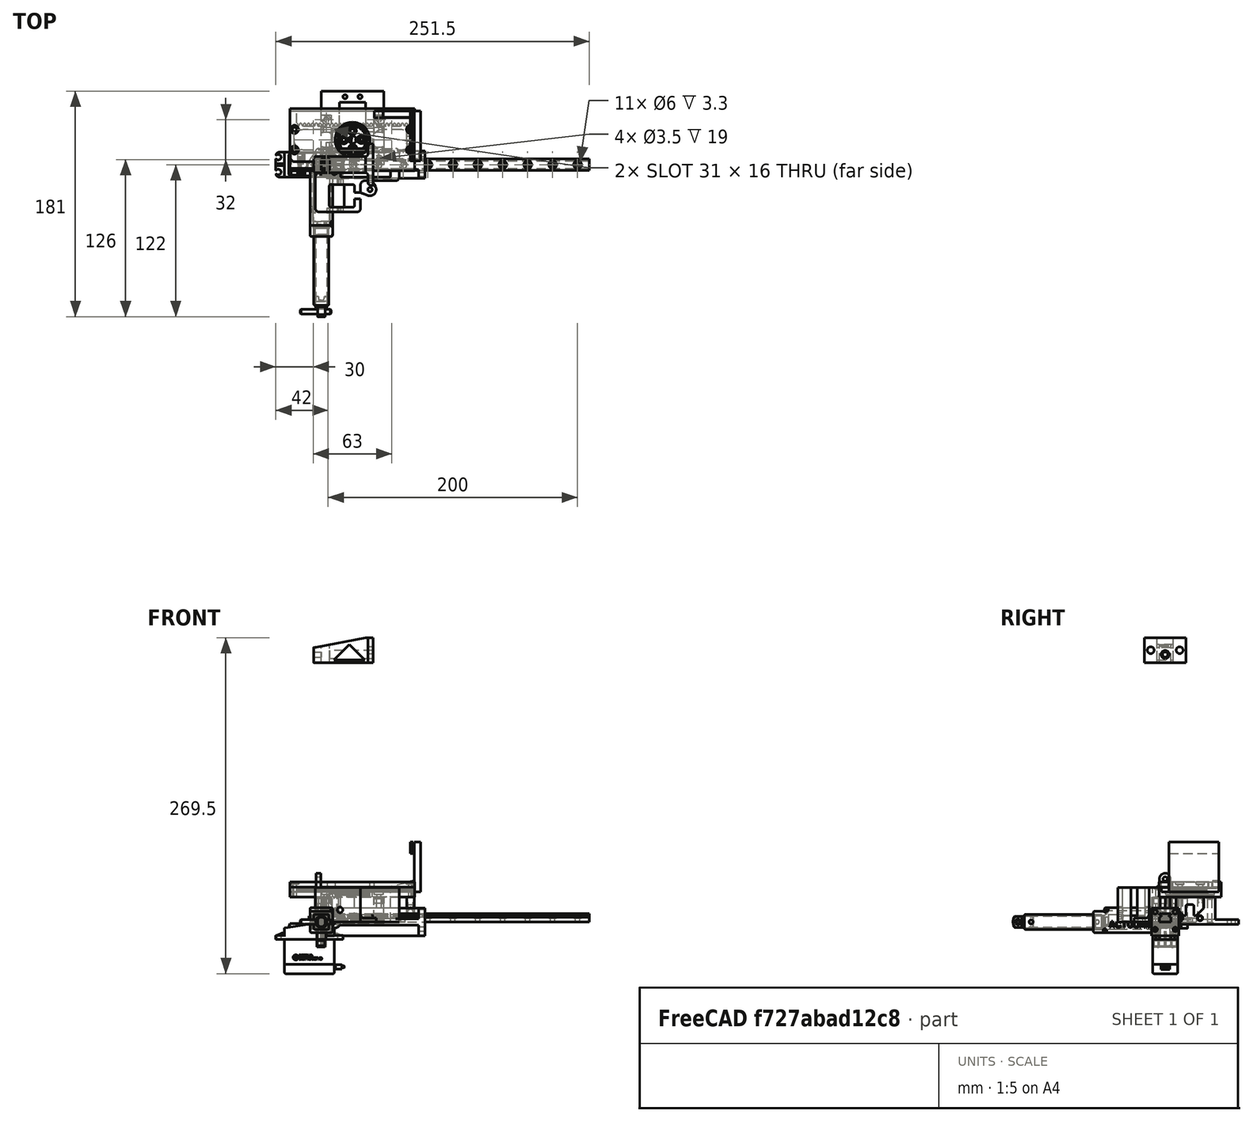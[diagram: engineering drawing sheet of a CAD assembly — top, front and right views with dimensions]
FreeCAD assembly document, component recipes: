
FREECAD ASSEMBLY — COMPONENT RECIPES ("PincePlanche")

This assembly document has 18 components, labeled P0..P17 below (a component is one placed body or linked part). 16 of them carry a construction recipe — the FreeCAD feature program that regenerates the part from scratch, quoted from this document or its linked companion documents; the rest are supplied as boundary geometry only. No exploded tour is included for this assembly.
COMPONENT P0 — recipe-attached ("support_pince_planche_bas", modeled in this document).
Construction recipe (the document's own serialized feature program — sketch geometry with constraints, then the solid features built on it; lengths are millimeters unless a unit is written):

FEATURE [Sketcher::SketchObject] Sketch042
  ArcFitTolerance = 1e-06
  AttachmentSupport = -> [XY_Plane019]
  FullyConstrained = true
  MakeInternals = false
  MapMode = 5
  Placement = pos=(0,0,0) rot=(0,1,0;3.14159rad)
  expr: Constraints[36] = 20 mm + VarSet.jeu
  expr: Constraints[37] = 40 mm + VarSet.jeu
  expr: Constraints[72] = 18 mm + VarSet.jeu
  expr: Constraints[73] = 20 mm + VarSet.jeu
  expr: Constraints[86] = 9 mm + VarSet.jeu
  expr: Constraints[87] = 6.5 mm + VarSet.jeu
  sketch-geometry (52):
    g0: LineSegment StartX=-28.5 StartY=-38 StartZ=0 EndX=1.8 EndY=-38 EndZ=0
    g1: LineSegment StartX=4.8 StartY=-35 StartZ=0 EndX=4.8 EndY=10 EndZ=0
    g2: ArcOfCircle CenterX=1.8 CenterY=-35 CenterZ=0 NormalX=0 NormalY=0 NormalZ=1 AngleXU=0 Radius=3 StartAngle=4.71239 EndAngle=6.28319
    g3: ArcOfCircle CenterX=1.8 CenterY=10 CenterZ=0 NormalX=0 NormalY=0 NormalZ=1 AngleXU=0 Radius=3 StartAngle=0 EndAngle=1.5708
    g4: GeomPoint [constr] X=4.8 Y=-38 Z=0
    g5: LineSegment StartX=-59.5 StartY=-13 StartZ=0 EndX=-34.5 EndY=-13 EndZ=0
    g6: LineSegment StartX=1.8 StartY=13 StartZ=0 EndX=-59.5 EndY=13 EndZ=0
    g7: ArcOfCircle CenterX=-59.5 CenterY=10 CenterZ=0 NormalX=0 NormalY=0 NormalZ=1 AngleXU=0 Radius=3 StartAngle=1.5708 EndAngle=3.14159
    g8: ArcOfCircle CenterX=-59.5 CenterY=-10 CenterZ=0 NormalX=0 NormalY=0 NormalZ=1 AngleXU=0 Radius=3 StartAngle=3.14159 EndAngle=4.71239
    g9: LineSegment StartX=-54.575 StartY=-10.075 StartZ=0 EndX=-16.425 EndY=-10.075 EndZ=0
    g10: LineSegment StartX=-15.425 StartY=-9.075 StartZ=0 EndX=-15.425 EndY=9.075 EndZ=0
    g11: LineSegment StartX=-16.425 StartY=10.075 StartZ=0 EndX=-54.575 EndY=10.075 EndZ=0
    g12: ArcOfCircle CenterX=-54.575 CenterY=9.075 CenterZ=0 NormalX=0 NormalY=0 NormalZ=1 AngleXU=0 Radius=1 StartAngle=1.5708 EndAngle=3.14159
    g13: ArcOfCircle CenterX=-54.575 CenterY=-9.075 CenterZ=0 NormalX=0 NormalY=0 NormalZ=1 AngleXU=0 Radius=1 StartAngle=3.14159 EndAngle=4.71239
    g14: ArcOfCircle CenterX=-16.425 CenterY=-9.075 CenterZ=0 NormalX=0 NormalY=0 NormalZ=1 AngleXU=0 Radius=1 StartAngle=4.71239 EndAngle=6.28319
    g15: ArcOfCircle CenterX=-16.425 CenterY=9.075 CenterZ=0 NormalX=0 NormalY=0 NormalZ=1 AngleXU=0 Radius=1 StartAngle=0 EndAngle=1.5708
    g16: GeomPoint [constr] X=-55.575 Y=10.075 Z=0
    g17: GeomPoint [constr] X=-15.425 Y=-10.075 Z=0
    g18: GeomPoint X=-35.5 Y=0 Z=0
    g19: ArcOfCircle CenterX=-34.5 CenterY=-16 CenterZ=0 NormalX=0 NormalY=0 NormalZ=1 AngleXU=0 Radius=3 StartAngle=0 EndAngle=1.5708
    g20: LineSegment StartX=-31.5 StartY=-16 StartZ=0 EndX=-31.5 EndY=-22.5 EndZ=0
    g21: ArcOfCircle CenterX=-28.5 CenterY=-35 CenterZ=0 NormalX=0 NormalY=0 NormalZ=1 AngleXU=0 Radius=3 StartAngle=3.14159 EndAngle=4.71239
    g22: GeomPoint [constr] X=-31.5 Y=-38 Z=0
    g23: GeomPoint X=-16.5 Y=-25 Z=0
    g24: LineSegment StartX=-26.575 StartY=-17.125 StartZ=0 EndX=-26.575 EndY=-22.5 EndZ=0
    g25: LineSegment StartX=-25.375 StartY=-34.075 StartZ=0 EndX=-7.625 EndY=-34.075 EndZ=0
    g26: LineSegment StartX=-6.425 StartY=-32.875 StartZ=0 EndX=-6.425 EndY=-17.125 EndZ=0
    g27: LineSegment StartX=-7.625 StartY=-15.925 StartZ=0 EndX=-25.375 EndY=-15.925 EndZ=0
    g28: ArcOfCircle CenterX=-25.375 CenterY=-17.125 CenterZ=0 NormalX=0 NormalY=0 NormalZ=1 AngleXU=0 Radius=1.2 StartAngle=1.5708 EndAngle=3.14159
    g29: ArcOfCircle CenterX=-25.375 CenterY=-32.875 CenterZ=0 NormalX=0 NormalY=0 NormalZ=1 AngleXU=0 Radius=1.2 StartAngle=3.14159 EndAngle=4.71239
    g30: ArcOfCircle CenterX=-7.625 CenterY=-32.875 CenterZ=0 NormalX=0 NormalY=0 NormalZ=1 AngleXU=0 Radius=1.2 StartAngle=4.71239 EndAngle=6.28319
    g31: ArcOfCircle CenterX=-7.625 CenterY=-17.125 CenterZ=0 NormalX=0 NormalY=0 NormalZ=1 AngleXU=0 Radius=1.2 StartAngle=-9e-16 EndAngle=1.5708
    g32: GeomPoint [constr] X=-26.575 Y=-15.925 Z=0
    g33: GeomPoint [constr] X=-6.425 Y=-34.075 Z=0
    g34: LineSegment StartX=-6.575 StartY=4.575 StartZ=0 EndX=-6.575 EndY=-4.575 EndZ=0
    g35: LineSegment StartX=-6.575 StartY=-4.575 StartZ=0 EndX=0.075 EndY=-4.575 EndZ=0
    g36: LineSegment StartX=0.075 StartY=-4.575 StartZ=0 EndX=0.075 EndY=4.575 EndZ=0
    g37: LineSegment StartX=0.075 StartY=4.575 StartZ=0 EndX=-6.575 EndY=4.575 EndZ=0
    g38: GeomPoint X=-3.25 Y=0 Z=0
    g39: LineSegment StartX=-26.575 StartY=-22.5 StartZ=0 EndX=-31.5 EndY=-22.5 EndZ=0
    g40: LineSegment StartX=-31.5 StartY=-27.5 StartZ=0 EndX=-26.575 EndY=-27.5 EndZ=0
    g41: LineSegment StartX=-26.575 StartY=-27.5 StartZ=0 EndX=-26.575 EndY=-32.875 EndZ=0
    g42: LineSegment StartX=-31.5 StartY=-27.5 StartZ=0 EndX=-31.5 EndY=-35 EndZ=0
    g43: LineSegment [constr] StartX=-16.5 StartY=-25 StartZ=0 EndX=-31.5 EndY=-25 EndZ=0
    g44: LineSegment StartX=-62.5 StartY=4 StartZ=0 EndX=-55.575 EndY=4 EndZ=0
    g45: LineSegment StartX=-62.5 StartY=-4 StartZ=0 EndX=-55.575 EndY=-4 EndZ=0
    g46: LineSegment StartX=-55.575 StartY=-4 StartZ=0 EndX=-55.575 EndY=-9.075 EndZ=0
    g47: LineSegment StartX=-62.5 StartY=-4 StartZ=0 EndX=-62.5 EndY=-10 EndZ=0
    g48: LineSegment StartX=-62.5 StartY=10 StartZ=0 EndX=-62.5 EndY=4 EndZ=0
    g49: LineSegment StartX=-55.575 StartY=9.075 StartZ=0 EndX=-55.575 EndY=4 EndZ=0
    g50: Circle CenterX=-10.5 CenterY=6 CenterZ=0 NormalX=0 NormalY=0 NormalZ=1 AngleXU=0 Radius=1.75
    g51: Circle CenterX=-10.5 CenterY=-6 CenterZ=0 NormalX=0 NormalY=0 NormalZ=1 AngleXU=0 Radius=1.75
  constraints (130):
    c: Tangent(g0,g2) = -1.5708
    c: Tangent(g1,g2) = -1.5708
    c: Tangent(g1,g3) = -1.5708
    c: Vertical(g1)
    c: Horizontal(g0)
    c: Equal(g2,g3)
    c: PointOnObject(g4,g0)
    c: PointOnObject(g4,g1)
    c: DistanceX(g-1,g1) = 4.8
    c: Tangent(g5,g8) = -1.5708
    c: Tangent(g6,g7) = -1.5708
    c: Horizontal(g5)
    c: Horizontal(g6)
    c: Equal(g7,g8)
    c: DistanceY(g5,g6) = 26
    c: Symmetric(g7,g47,g-1)
    c: Radius(g7) = 3
    c: Tangent(g3,g6) = -1.5708
    c: Tangent(g9,g13) = -1.5708
    c: Tangent(g9,g14) = -1.5708
    c: Tangent(g10,g14) = -1.5708
    c: Tangent(g10,g15) = -1.5708
    c: Tangent(g11,g15) = -1.5708
    c: Tangent(g11,g12) = -1.5708
    c: Vertical(g10)
    c: Horizontal(g9)
    c: Horizontal(g11)
    c: Equal(g12,g13)
    c: Equal(g13,g14)
    c: Equal(g14,g15)
    c: PointOnObject(g16,g11)
    c: PointOnObject(g17,g9)
    c: PointOnObject(g17,g10)
    c: Radius(g13) = 1
    c: PointOnObject(g18,g-1)
    c: Symmetric(g16,g17,g18)
    c: DistanceY(g9,g11) = 20.15
    c: DistanceX(g12,g10) = 40.15
    c: DistanceX(g18,g-1) = 35.5
    c: DistanceX(g7,g18) = 27
    c: Vertical(g20)
    c: PointOnObject(g22,g42)
    c: PointOnObject(g22,g0)
    c: Tangent(g0,g21) = -1.5708
    c: Tangent(g19,g5) = 1.5708
    c: Tangent(g20,g19) = 1.5708
    c: DistanceY(g23,g-1) = 25
    c: DistanceX(g23,g-1) = 16.5
    c: DistanceX(g19,g23) = 15
    c: DistanceY(g0,g23) = 13
    c: Equal(g21,g19)
    c: Equal(g19,g2)
    c: Equal(g3,g7)
    c: Tangent(g24,g28) = -1.5708
    c: Tangent(g25,g29) = -1.5708
    c: Tangent(g25,g30) = -1.5708
    c: Tangent(g26,g30) = -1.5708
    c: Tangent(g26,g31) = -1.5708
    c: Tangent(g27,g31) = -1.5708
    c: Tangent(g27,g28) = -1.5708
    c: Vertical(g24)
    c: Vertical(g26)
    c: Horizontal(g25)
    c: Horizontal(g27)
    c: Equal(g28,g29)
    c: Equal(g29,g30)
    c: Equal(g30,g31)
    c: PointOnObject(g32,g24)
    c: PointOnObject(g32,g27)
    c: PointOnObject(g33,g25)
    c: PointOnObject(g33,g26)
    c: Symmetric(g33,g32,g23)
    c: DistanceY(g25,g27) = 18.15
    c: DistanceX(g24,g26) = 20.15
    c: Radius(g31) = 1.2
    c: Coincident(g34,g35)
    c: Coincident(g35,g36)
    c: Coincident(g36,g37)
    c: Coincident(g37,g34)
    c: Vertical(g34)
    c: Vertical(g36)
    c: Horizontal(g35)
    c: Horizontal(g37)
    c: PointOnObject(g38,g-1)
    c: Symmetric(g36,g34,g38)
    c: DistanceX(g38,g-1) = 3.25
    c: DistanceY(g34,g34) = 9.15
    c: DistanceX(g37,g37) = 6.65
    c: Horizontal(g39)
    c: Horizontal(g40)
    c: PointOnObject(g40,g41)
    c: PointOnObject(g40,g42)
    c: Coincident(g24,g39)
    c: PointOnObject(g41,g40)
    c: Coincident(g20,g39)
    c: PointOnObject(g42,g40)
    c: Coincident(g43,g23)
    c: Horizontal(g43)
    c: Symmetric(g20,g40,g43)
    c: Vertical(g24,g40)
    c: Vertical(g40,g20)
    c: DistanceY(g40,g24) = 5
    c: Vertical(g41)
    c: Tangent(g41,g29) = -1.5708
    c: Tangent(g42,g21) = -1.5708
    c: Vertical(g42)
    c: Horizontal(g44)
    c: PointOnObject(g45,g47)
    c: Horizontal(g45)
    c: PointOnObject(g45,g46)
    c: PointOnObject(g46,g45)
    c: PointOnObject(g47,g45)
    c: Coincident(g48,g44)
    c: Vertical(g48)
    c: Tangent(g7,g48) = -1.5708
    c: Tangent(g47,g8) = -1.5708
    c: Tangent(g46,g13) = -1.5708
    c: Vertical(g46)
    c: Vertical(g47)
    c: Coincident(g49,g44)
    c: Vertical(g49)
    c: Tangent(g49,g12) = -1.5708
    c: Symmetric(g44,g45,g-1)
    c: Vertical(g16,g12)
    c: DistanceY(g45,g44) = 8
    c: Symmetric(g50,g51,g-1)
    c: DistanceX(g18,g51) = 25
    c: DistanceY(g18,g50) = 6
    c: Equal(g50,g51)
    c: Diameter(g50) = 3.5
FEATURE [PartDesign::Pad] Pad015
  Direction = (0,0,-1)
  Length = 27.5
  Length2 = 10
  Profile = -> Sketch042
  ReferenceAxis = -> Sketch042 [N_Axis]
  Reversed = true
  Suppressed = false
  Type = 0
FEATURE [Sketcher::SketchObject] Sketch055
  ArcFitTolerance = 1e-06
  AttachmentSupport = -> [XY_Plane019]
  ExternalGeometry = -> [Pad015]
  FullyConstrained = true
  MakeInternals = false
  MapMode = 5
  Placement = pos=(0,0,0) rot=(0,1,0;3.14159rad)
  sketch-geometry (8):
    g0: LineSegment StartX=-6.575 StartY=4.575 StartZ=0 EndX=-6.575 EndY=-4.575 EndZ=0
    g1: LineSegment StartX=-6.575 StartY=-4.575 StartZ=0 EndX=0.075 EndY=-4.575 EndZ=0
    g2: LineSegment StartX=0.075 StartY=-4.575 StartZ=0 EndX=0.075 EndY=4.575 EndZ=0
    g3: LineSegment StartX=0.075 StartY=4.575 StartZ=0 EndX=-6.575 EndY=4.575 EndZ=0
    g4: LineSegment StartX=-18.425 StartY=-15.925 StartZ=0 EndX=-18.425 EndY=-34.075 EndZ=0
    g5: LineSegment StartX=-18.425 StartY=-34.075 StartZ=0 EndX=-6.425 EndY=-34.075 EndZ=0
    g6: LineSegment StartX=-6.425 StartY=-34.075 StartZ=0 EndX=-6.425 EndY=-15.925 EndZ=0
    g7: LineSegment StartX=-6.425 StartY=-15.925 StartZ=0 EndX=-18.425 EndY=-15.925 EndZ=0
  constraints (22):
    c: Coincident(g0,g1)
    c: Coincident(g1,g2)
    c: Coincident(g2,g3)
    c: Coincident(g3,g0)
    c: Vertical(g0)
    c: Vertical(g2)
    c: Horizontal(g1)
    c: Horizontal(g3)
    c: Coincident(g4,g5)
    c: Coincident(g5,g6)
    c: Coincident(g6,g7)
    c: Coincident(g7,g4)
    c: Vertical(g4)
    c: Vertical(g6)
    c: Horizontal(g5)
    c: Horizontal(g7)
    c: PointOnObject(g4,g-5)
    c: PointOnObject(g6,g-6)
    c: PointOnObject(g5,g-7)
    c: DistanceX(g7,g7) = 12
    c: Coincident(g0,g-3)
    c: Coincident(g1,g-4)
FEATURE [PartDesign::Pad] Pad023
  BaseFeature = -> Pad015
  Direction = (0,0,-1)
  Length = 5
  Length2 = 10
  Profile = -> Sketch055
  ReferenceAxis = -> Sketch055 [N_Axis]
  Reversed = true
  Suppressed = false
  Type = 0
FEATURE [Sketcher::SketchObject] Sketch056
  ArcFitTolerance = 1e-06
  AttachmentOffset = pos=(0,0,-0.25) rot=(0,0,1;0rad)
  AttachmentSupport = -> [YZ_Plane019]
  ExternalGeometry = -> [Pad023]
  FullyConstrained = true
  MakeInternals = false
  MapMode = 5
  Placement = pos=(-0.25,0,0) rot=(0.57735,0.57735,0.57735;2.0944rad)
  sketch-geometry (7):
    g0: LineSegment StartX=-8.575 StartY=27.5 StartZ=0 EndX=8.575 EndY=27.5 EndZ=0
    g1: LineSegment StartX=4.575 StartY=31.5 StartZ=0 EndX=4.575 EndY=34.5 EndZ=0
    g2: LineSegment StartX=-4.575 StartY=34.5 StartZ=0 EndX=-4.575 EndY=31.5 EndZ=0
    g3: ArcOfCircle CenterX=0 CenterY=34.5 CenterZ=0 NormalX=0 NormalY=0 NormalZ=1 AngleXU=0 Radius=4.575 StartAngle=0 EndAngle=3.14159
    g4: Circle CenterX=0 CenterY=34.5 CenterZ=0 NormalX=0 NormalY=0 NormalZ=1 AngleXU=0 Radius=1.75
    g5: ArcOfCircle CenterX=-8.575 CenterY=31.5 CenterZ=0 NormalX=0 NormalY=0 NormalZ=1 AngleXU=0 Radius=4 StartAngle=4.71239 EndAngle=6.28319
    g6: ArcOfCircle CenterX=8.575 CenterY=31.5 CenterZ=0 NormalX=0 NormalY=0 NormalZ=1 AngleXU=0 Radius=4 StartAngle=3.14159 EndAngle=4.71239
  constraints (17):
    c: Vertical(g1)
    c: Vertical(g2)
    c: PointOnObject(g3,g-2)
    c: DistanceY(g-1,g3) = 34.5
    c: Tangent(g3,g1) = -1.5708
    c: Coincident(g4,g3)
    c: Diameter(g4) = 3.5
    c: Tangent(g3,g2) = -1.5708
    c: Tangent(g2,g5) = 1.5708
    c: Tangent(g0,g5) = -1.5708
    c: Horizontal(g0,g-3)
    c: Vertical(g2,g-3)
    c: Horizontal(g0,g-3)
    c: Tangent(g6,g1) = 1.5708
    c: Tangent(g0,g6) = -1.5708
    c: Equal(g1,g2)
    c: Radius(g6) = 4
FEATURE [PartDesign::Pad] Pad024
  BaseFeature = -> Pad023
  Direction = (1,0,0)
  Length = 4
  Length2 = 10
  Profile = -> Sketch056
  ReferenceAxis = -> Sketch056 [N_Axis]
  Reversed = true
  Suppressed = false
  Type = 0
FEATURE [Sketcher::SketchObject] Sketch057
  ArcFitTolerance = 1e-06
  AttachmentSupport = -> [XY_Plane019]
  ExternalGeometry = -> [Pad024]
  FullyConstrained = true
  MakeInternals = false
  MapMode = 5
  sketch-geometry (14):
    g0: ArcOfCircle CenterX=34.5 CenterY=-16 CenterZ=0 NormalX=0 NormalY=0 NormalZ=1 AngleXU=0 Radius=3 StartAngle=1.5708 EndAngle=3.14159
    g1: ArcOfCircle CenterX=39 CenterY=-20 CenterZ=0 NormalX=0 NormalY=0 NormalZ=1 AngleXU=0 Radius=5 StartAngle=4.34942 EndAngle=6.76197
    g2: LineSegment StartX=31.5 StartY=-16 StartZ=0 EndX=31.5 EndY=-22.5 EndZ=0
    g3: LineSegment StartX=34.5 StartY=-13 StartZ=0 EndX=41 EndY=-13 EndZ=0
    g4: Circle CenterX=39 CenterY=-20 CenterZ=0 NormalX=0 NormalY=0 NormalZ=1 AngleXU=0 Radius=1.75
    g5: LineSegment StartX=31.5 StartY=-22.5 StartZ=0 EndX=37.2247 EndY=-24.6742 EndZ=0
    g6: LineSegment StartX=43.4378 StartY=-17.6965 StartZ=0 EndX=41 EndY=-13 EndZ=0
    g7: Circle CenterX=29.2 CenterY=20 CenterZ=0 NormalX=0 NormalY=0 NormalZ=1 AngleXU=0 Radius=1.75
    g8: LineSegment StartX=20.2 StartY=13 StartZ=0 EndX=38.2 EndY=13 EndZ=0
    g9: LineSegment StartX=34.2 StartY=17 StartZ=0 EndX=34.2 EndY=20 EndZ=0
    g10: LineSegment StartX=24.2 StartY=17 StartZ=0 EndX=24.2 EndY=20 EndZ=0
    g11: ArcOfCircle CenterX=29.2 CenterY=20 CenterZ=0 NormalX=0 NormalY=0 NormalZ=1 AngleXU=0 Radius=5 StartAngle=0 EndAngle=3.14159
    g12: ArcOfCircle CenterX=20.2 CenterY=17 CenterZ=0 NormalX=0 NormalY=0 NormalZ=1 AngleXU=0 Radius=4 StartAngle=4.71239 EndAngle=6.28319
    g13: ArcOfCircle CenterX=38.2 CenterY=17 CenterZ=0 NormalX=0 NormalY=0 NormalZ=1 AngleXU=0 Radius=4 StartAngle=3.14159 EndAngle=4.71239
  constraints (34):
    c: Coincident(g0,g-3)
    c: Coincident(g3,g0)
    c: Horizontal(g3)
    c: Vertical(g2)
    c: Tangent(g2,g0) = -1.5708
    c: Coincident(g0,g-3)
    c: Coincident(g4,g1)
    c: Diameter(g4) = 3.5
    c: Radius(g1) = 5
    c: Coincident(g2,g5)
    c: Tangent(g5,g1) = -1.5708
    c: Coincident(g6,g3)
    c: Tangent(g6,g1) = -1.5708
    c: Equal(g3,g2)
    c: DistanceX(g3,g3) = 6.5
    c: Horizontal(g8)
    c: Vertical(g9)
    c: Vertical(g10)
    c: PointOnObject(g8,g-4)
    c: Coincident(g7,g11)
    c: Tangent(g11,g9) = -1.5708
    c: Tangent(g11,g10) = 1.5708
    c: Tangent(g10,g12) = -1.5708
    c: Tangent(g8,g12) = -1.5708
    c: Tangent(g13,g9) = 1.5708
    c: Tangent(g13,g8) = -1.5708
    c: Diameter(g7) = 3.5
    c: Equal(g11,g1)
    c: Equal(g10,g9)
    c: Radius(g13) = 4
    c: DistanceY(g-1,g7) = 20
    c: DistanceX(g-1,g7) = 29.2
    c: DistanceY(g1,g-1) = 20
    c: DistanceX(g-1,g1) = 39
FEATURE [PartDesign::Pad] Pad025
  BaseFeature = -> Pad024
  Direction = (0,0,1)
  Length = 3
  Length2 = 10
  Profile = -> Sketch057
  ReferenceAxis = -> Sketch057 [N_Axis]
  Suppressed = false
  Type = 0
FEATURE [Sketcher::SketchObject] Sketch058
  ArcFitTolerance = 1e-06
  AttachmentOffset = pos=(15,9.6,25) rot=(0,0,1;0rad)
  AttachmentSupport = -> [XZ_Plane019]
  FullyConstrained = true
  MakeInternals = false
  MapMode = 5
  Placement = pos=(15,-25,9.6) rot=(1,0,0;1.5708rad)
  sketch-geometry (2):
    g0: ArcOfCircle CenterX=0 CenterY=0 CenterZ=0 NormalX=0 NormalY=0 NormalZ=1 AngleXU=0 Radius=2.25 StartAngle=1.99427 EndAngle=7.43051
    g1: ArcOfCircle CenterX=0 CenterY=1 CenterZ=0 NormalX=0 NormalY=0 NormalZ=1 AngleXU=0 Radius=1.4 StartAngle=0.849413 EndAngle=2.29218
  constraints (7):
    c: Coincident(g0,g-1)
    c: Diameter(g0) = 4.5
    c: Coincident(g1,g0)
    c: Coincident(g1,g0)
    c: PointOnObject(g1,g-2)
    c: DistanceY(g0,g1) = 1
    c: Radius(g1) = 1.4
FEATURE [PartDesign::Pocket] Pocket028
  BaseFeature = -> Pad025
  Direction = (0,1,-2e-16)
  Length = 27
  Length2 = 5
  Midplane = true
  Profile = -> Sketch058
  ReferenceAxis = -> Sketch058 [N_Axis]
  Suppressed = false
  Type = 0
FEATURE [Sketcher::SketchObject] Sketch059
  ArcFitTolerance = 1e-06
  AttachmentSupport = -> [Pocket028]
  ExternalGeometry = -> [Pocket028]
  FullyConstrained = true
  MakeInternals = false
  MapMode = 5
  Placement = pos=(0,0,27.5) rot=(0,0,1;0rad)
  sketch-geometry (2):
    g0: Circle CenterX=10.5 CenterY=6 CenterZ=0 NormalX=0 NormalY=0 NormalZ=1 AngleXU=0 Radius=2.1
    g1: Circle CenterX=10.5 CenterY=-6 CenterZ=0 NormalX=0 NormalY=0 NormalZ=1 AngleXU=0 Radius=2.1
  constraints (4):
    c: Coincident(g0,g-3)
    c: Coincident(g1,g-4)
    c: Equal(g0,g1)
    c: Diameter(g0) = 4.2
FEATURE [PartDesign::Pocket] Pocket029
  BaseFeature = -> Pocket028
  Direction = (0,0,-1)
  Length = 1.5
  Length2 = 5
  Profile = -> Sketch059
  ReferenceAxis = -> Sketch059 [N_Axis]
  Suppressed = false
  Type = 0
FEATURE [PartDesign::Fillet] Fillet
  Base = -> Pocket029 [Edge169,Edge108]
  BaseFeature = -> Pocket029
  Radius = 3
  SupportTransform = false
  Suppressed = false
  UseAllEdges = false
FEATURE [PartDesign::Body] Body013  label="support_pince_planche_bas"
  AllowCompound = false
  Group = -> [Sketch042,Pad015,Sketch055,Pad023,Sketch056,Pad024,Sketch057,Pad025,Sketch058,Pocket028,Sketch059,Pocket029,Fillet]
  Origin = -> Origin019
  Tip = -> Fillet
COMPONENT P1 — recipe-attached ("support_pince_planche_haut", modeled in this document).
Construction recipe (the document's own serialized feature program — sketch geometry with constraints, then the solid features built on it; lengths are millimeters unless a unit is written):

FEATURE [Sketcher::SketchObject] Sketch063
  ArcFitTolerance = 1e-06
  AttachmentSupport = -> [XY_Plane024]
  FullyConstrained = true
  MakeInternals = false
  MapMode = 5
  sketch-geometry (11):
    g0: LineSegment StartX=-3.15 StartY=4.65 StartZ=0 EndX=-3.15 EndY=-4.65 EndZ=0
    g1: LineSegment StartX=-3.15 StartY=-4.65 StartZ=0 EndX=3.15 EndY=-4.65 EndZ=0
    g2: LineSegment StartX=3.15 StartY=-4.65 StartZ=0 EndX=3.15 EndY=4.65 EndZ=0
    g3: LineSegment StartX=3.15 StartY=4.65 StartZ=0 EndX=-3.15 EndY=4.65 EndZ=0
    g4: LineSegment StartX=-6.15 StartY=4.65 StartZ=0 EndX=-6.15 EndY=-4.65 EndZ=0
    g5: LineSegment StartX=-3.15 StartY=-7.65 StartZ=0 EndX=38.5 EndY=-7.65 EndZ=0
    g6: LineSegment StartX=38.5 StartY=-7.65 StartZ=0 EndX=38.5 EndY=7.65 EndZ=0
    g7: LineSegment StartX=38.5 StartY=7.65 StartZ=0 EndX=-3.15 EndY=7.65 EndZ=0
    g8: ArcOfCircle CenterX=-3.15 CenterY=4.65 CenterZ=0 NormalX=0 NormalY=0 NormalZ=1 AngleXU=0 Radius=3 StartAngle=1.5708 EndAngle=3.14159
    g9: ArcOfCircle CenterX=-3.15 CenterY=-4.65 CenterZ=0 NormalX=0 NormalY=0 NormalZ=1 AngleXU=0 Radius=3 StartAngle=3.14159 EndAngle=4.71239
    g10: GeomPoint [constr] X=-6.15 Y=7.65 Z=0
  constraints (27):
    c: Coincident(g0,g1)
    c: Coincident(g1,g2)
    c: Coincident(g2,g3)
    c: Coincident(g3,g0)
    c: Vertical(g0)
    c: Vertical(g2)
    c: Horizontal(g1)
    c: Horizontal(g3)
    c: Tangent(g4,g8) = -1.5708
    c: Tangent(g4,g9) = -1.5708
    c: Tangent(g5,g9) = -1.5708
    c: Tangent(g7,g8) = -1.5708
    c: Vertical(g4)
    c: Horizontal(g5)
    c: Horizontal(g7)
    c: Equal(g8,g9)
    c: PointOnObject(g10,g4)
    c: PointOnObject(g10,g7)
    c: Radius(g9) = 3
    c: Coincident(g6,g7)
    c: Coincident(g5,g6)
    c: Symmetric(g6,g5,g-1)
    c: Symmetric(g2,g0,g-1)
    c: DistanceY(g0,g0) = 9.3
    c: DistanceX(g3,g3) = 6.3
    c: Coincident(g0,g8)
    c: DistanceX(g-1,g6) = 38.5
FEATURE [PartDesign::Pad] Pad029
  Direction = (0,0,1)
  Length = 5
  Length2 = 10
  Profile = -> Sketch063
  ReferenceAxis = -> Sketch063 [N_Axis]
  Suppressed = false
  Type = 0
FEATURE [Sketcher::SketchObject] Sketch064
  ArcFitTolerance = 1e-06
  AttachmentSupport = -> [Pad029]
  ExternalGeometry = -> [Pad029]
  FullyConstrained = true
  MakeInternals = false
  MapMode = 5
  Placement = pos=(38.5,0,0) rot=(0.57735,0.57735,0.57735;2.0944rad)
  sketch-geometry (8):
    g0: Circle CenterX=0 CenterY=16 CenterZ=0 NormalX=0 NormalY=0 NormalZ=1 AngleXU=0 Radius=2.75
    g1: LineSegment StartX=-7.65 StartY=19 StartZ=0 EndX=-7.65 EndY=5 EndZ=0
    g2: LineSegment StartX=7.65 StartY=5 StartZ=0 EndX=7.65 EndY=19 EndZ=0
    g3: LineSegment StartX=4.65 StartY=22 StartZ=0 EndX=-4.65 EndY=22 EndZ=0
    g4: ArcOfCircle CenterX=-4.65 CenterY=19 CenterZ=0 NormalX=0 NormalY=0 NormalZ=1 AngleXU=0 Radius=3 StartAngle=1.5708 EndAngle=3.14159
    g5: ArcOfCircle CenterX=4.65 CenterY=19 CenterZ=0 NormalX=0 NormalY=0 NormalZ=1 AngleXU=0 Radius=3 StartAngle=-9e-16 EndAngle=1.5708
    g6: GeomPoint [constr] X=-7.65 Y=22 Z=0
    g7: LineSegment StartX=-7.65 StartY=5 StartZ=0 EndX=7.65 EndY=5 EndZ=0
  constraints (19):
    c: Diameter(g0) = 5.5
    c: PointOnObject(g0,g-2)
    c: Tangent(g1,g4) = -1.5708
    c: Tangent(g2,g5) = -1.5708
    c: Tangent(g3,g5) = -1.5708
    c: Tangent(g3,g4) = -1.5708
    c: Vertical(g1)
    c: Vertical(g2)
    c: Horizontal(g3)
    c: PointOnObject(g6,g1)
    c: PointOnObject(g6,g3)
    c: Coincident(g1,g-3)
    c: Coincident(g2,g-3)
    c: Equal(g5,g4)
    c: Radius(g4) = 3
    c: DistanceY(g2,g0) = 11
    c: Coincident(g7,g1)
    c: Coincident(g7,g2)
    c: DistanceY(g0,g3) = 6
FEATURE [PartDesign::Pad] Pad030
  BaseFeature = -> Pad029
  Direction = (1,0,0)
  Length = 3
  Length2 = 10
  Profile = -> Sketch064
  ReferenceAxis = -> Sketch064 [N_Axis]
  Reversed = true
  Suppressed = false
  Type = 0
FEATURE [PartDesign::Chamfer] Chamfer  label="Chamfer001"
  Angle = 45
  Base = -> Pad030 [Edge19]
  BaseFeature = -> Pad030
  ChamferType = 1
  FlipDirection = false
  Size = 15
  Size2 = 5
  SupportTransform = false
  Suppressed = false
  UseAllEdges = false
FEATURE [PartDesign::Body] Body017  label="support_pince_planche_haut"
  AllowCompound = false
  Group = -> [Sketch063,Pad029,Sketch064,Pad030,Chamfer]
  Origin = -> Origin024
  Placement = pos=(3,-2.563e-05,214) rot=(0,0,1;0rad)
  Tip = -> Chamfer
COMPONENT P2 — recipe-attached ("support_rail_haut", modeled in this document).
Construction recipe (the document's own serialized feature program — sketch geometry with constraints, then the solid features built on it; lengths are millimeters unless a unit is written):

FEATURE [Sketcher::SketchObject] Sketch236
  ArcFitTolerance = 1e-06
  AttachmentSupport = -> [XZ_Plane278]
  FullyConstrained = true
  MakeInternals = false
  MapMode = 5
  Placement = pos=(0,0,0) rot=(1,0,0;1.5708rad)
  sketch-geometry (18):
    g0: LineSegment StartX=-4.5 StartY=0 StartZ=0 EndX=-4.5 EndY=-6 EndZ=0
    g1: LineSegment StartX=-4.5 StartY=-6 StartZ=0 EndX=12.3701 EndY=-6 EndZ=0
    g2: LineSegment StartX=17.2308 StartY=0.172017 StartZ=0 EndX=8.52786 EndY=36.2656 EndZ=0
    g3: LineSegment StartX=9.5 StartY=37.5 StartZ=0 EndX=21.5 EndY=37.5 EndZ=0
    g4: LineSegment StartX=21.5 StartY=37.5 StartZ=0 EndX=21.5 EndY=41.5 EndZ=0
    g5: LineSegment StartX=21.5 StartY=41.5 StartZ=0 EndX=8.47134 EndY=41.5 EndZ=0
    g6: LineSegment StartX=3.61064 StartY=35.328 StartZ=0 EndX=10.2 EndY=8 EndZ=0
    g7: LineSegment StartX=10.2 StartY=0 StartZ=0 EndX=-4.5 EndY=0 EndZ=0
    g8: ArcOfCircle CenterX=9.5 CenterY=36.5 CenterZ=0 NormalX=0 NormalY=0 NormalZ=1 AngleXU=0 Radius=1 StartAngle=1.5708 EndAngle=3.3782
    g9: GeomPoint [constr] X=8.23022 Y=37.5 Z=0
    g10: GeomPoint [constr] X=12.129 Y=0 Z=0
    g11: ArcOfCircle CenterX=12.3701 CenterY=-1 CenterZ=0 NormalX=0 NormalY=0 NormalZ=1 AngleXU=0 Radius=5 StartAngle=4.71239 EndAngle=6.51979
    g12: GeomPoint [constr] X=18.719 Y=-6 Z=0
    g13: GeomPoint X=15.5 Y=37.5 Z=0
    g14: LineSegment [constr] StartX=10.2 StartY=8 StartZ=0 EndX=15.0607 EndY=9.17202 EndZ=0
    g15: ArcOfCircle CenterX=8.47134 CenterY=36.5 CenterZ=0 NormalX=0 NormalY=0 NormalZ=1 AngleXU=0 Radius=5 StartAngle=1.5708 EndAngle=3.3782
    g16: GeomPoint [constr] X=2.12244 Y=41.5 Z=0
    g17: LineSegment StartX=10.2 StartY=0 StartZ=0 EndX=10.2 EndY=8 EndZ=0
  constraints (45):
    c: PointOnObject(g0,g-1)
    c: Vertical(g0)
    c: Coincident(g0,g1)
    c: Horizontal(g1)
    c: Horizontal(g3)
    c: Coincident(g3,g4)
    c: Vertical(g4)
    c: Coincident(g4,g5)
    c: Horizontal(g5)
    c: PointOnObject(g10,g-1)
    c: Coincident(g7,g0)
    c: DistanceY(g4,g4) = 4
    c: PointOnObject(g9,g3)
    c: PointOnObject(g9,g2)
    c: Tangent(g3,g8) = 1.5708
    c: Tangent(g2,g8) = 1.5708
    c: PointOnObject(g10,g6)
    c: PointOnObject(g10,g7)
    c: PointOnObject(g12,g1)
    c: PointOnObject(g12,g2)
    c: Tangent(g1,g11) = -1.5708
    c: Tangent(g2,g11) = -1.5708
    c: DistanceY(g0,g0) = 6
    c: DistanceX(g0,g-1) = 4.5
    c: Radius(g11) = 5
    c: Radius(g8) = 1
    c: DistanceX(g3,g3) = 12
    c: Symmetric(g3,g3,g13)
    c: DistanceX(g-1,g13) = 15.5
    c: DistanceY(g-1,g16) = 41.5
    c: Parallel(g2,g6)
    c: DistanceX(g-1,g7) = 10.2
    c: Coincident(g14,g6)
    c: PointOnObject(g14,g2)
    c: Perpendicular(g2,g14)
    c: Distance(g14,g14) = 5
    c: PointOnObject(g16,g5)
    c: PointOnObject(g16,g6)
    c: Tangent(g5,g15) = -1.5708
    c: Tangent(g6,g15) = -1.5708
    c: Radius(g15) = 5
    c: Coincident(g17,g7)
    c: Coincident(g17,g6)
    c: Vertical(g17)
    c: DistanceY(g17,g17) = 8
FEATURE [PartDesign::Pad] Pad114
  Direction = (0,-1,2e-16)
  Length = 13
  Length2 = 10
  Midplane = true
  Placement = pos=(0,0,0) rot=(1,0,0;1.5708rad)
  Profile = -> Sketch236
  ReferenceAxis = -> Sketch236 [N_Axis]
  Suppressed = false
  Type = 0
FEATURE [Sketcher::SketchObject] Sketch237
  ArcFitTolerance = 1e-06
  AttachmentSupport = -> [Pad114]
  ExternalGeometry = -> [Pad114]
  FullyConstrained = true
  MakeInternals = false
  MapMode = 5
  Placement = pos=(0,6.5,0) rot=(-1,0,0;1.5708rad)
  sketch-geometry (4):
    g0: LineSegment StartX=-4.5 StartY=0 StartZ=0 EndX=-4.5 EndY=-1.5 EndZ=0
    g1: LineSegment StartX=-4.5 StartY=-1.5 StartZ=0 EndX=12.5 EndY=-1.5 EndZ=0
    g2: LineSegment StartX=12.5 StartY=-1.5 StartZ=0 EndX=12.5 EndY=0 EndZ=0
    g3: LineSegment StartX=12.5 StartY=0 StartZ=0 EndX=-4.5 EndY=0 EndZ=0
  constraints (11):
    c: Coincident(g0,g1)
    c: Coincident(g1,g2)
    c: Coincident(g2,g3)
    c: Coincident(g3,g0)
    c: Vertical(g0)
    c: Vertical(g2)
    c: Horizontal(g1)
    c: Horizontal(g3)
    c: Coincident(g0,g-3)
    c: DistanceY(g0,g0) = 1.5
    c: DistanceX(g3,g3) = 17
FEATURE [PartDesign::Pad] Pad115
  BaseFeature = -> Pad114
  Direction = (0,1,2e-16)
  Length = 1.9
  Length2 = 10
  Placement = pos=(0,0,0) rot=(1,0,0;1.5708rad)
  Profile = -> Sketch237
  ReferenceAxis = -> Sketch237 [N_Axis]
  Refine = true
  Reversed = true
  Suppressed = false
  Type = 0
FEATURE [PartDesign::Mirrored] Mirrored010
  BaseFeature = -> Pad115
  MirrorPlane = -> XZ_Plane278
  Originals = -> [Pad115]
  Placement = pos=(0,0,0) rot=(1,0,0;1.5708rad)
  Refine = true
  Suppressed = false
  TransformMode = 0
FEATURE [Sketcher::SketchObject] Sketch235
  ArcFitTolerance = 1e-06
  AttachmentSupport = -> [Mirrored010]
  FullyConstrained = true
  MakeInternals = false
  MapMode = 5
  Placement = pos=(0,-2.6e-15,-6) rot=(1,0,0;3.14159rad)
  sketch-geometry (2):
    g0: Circle CenterX=0 CenterY=0 CenterZ=0 NormalX=0 NormalY=0 NormalZ=1 AngleXU=0 Radius=1.85
    g1: Circle CenterX=15.5 CenterY=0 CenterZ=0 NormalX=0 NormalY=0 NormalZ=1 AngleXU=0 Radius=2.75
  constraints (5):
    c: Diameter(g0) = 3.7
    c: Coincident(g0,g-1)
    c: Diameter(g1) = 5.5
    c: PointOnObject(g1,g-1)
    c: DistanceX(g-1,g1) = 15.5
FEATURE [PartDesign::Pocket] Pocket096
  BaseFeature = -> Mirrored010
  Direction = (0,0,1)
  Length = 5
  Length2 = 5
  Placement = pos=(0,0,0) rot=(1,0,0;1.5708rad)
  Profile = -> Sketch235
  ReferenceAxis = -> Sketch235 [N_Axis]
  Suppressed = false
  Type = 1
FEATURE [Sketcher::SketchObject] Sketch238
  ArcFitTolerance = 1e-06
  AttachmentSupport = -> [Pocket096]
  ExternalGeometry = -> [Pocket096]
  FullyConstrained = true
  MakeInternals = false
  MapMode = 5
  Placement = pos=(0,-2.6e-15,-6) rot=(1,0,0;3.14159rad)
  sketch-geometry (1):
    g0: Circle CenterX=0 CenterY=0 CenterZ=0 NormalX=0 NormalY=0 NormalZ=1 AngleXU=0 Radius=2.1
  constraints (2):
    c: Coincident(g0,g-1)
    c: Diameter(g0) = 4.2
FEATURE [PartDesign::Pocket] Pocket097
  BaseFeature = -> Pocket096
  Direction = (0,0,1)
  Length = 3
  Length2 = 5
  Placement = pos=(0,0,0) rot=(1,0,0;1.5708rad)
  Profile = -> Sketch238
  ReferenceAxis = -> Sketch238 [N_Axis]
  Suppressed = false
  Type = 0
FEATURE [Sketcher::SketchObject] Sketch239
  ArcFitTolerance = 1e-06
  AttachmentSupport = -> [Pocket097]
  FullyConstrained = true
  MakeInternals = false
  MapMode = 5
  Placement = pos=(0,-2.6e-15,-6) rot=(1,0,0;3.14159rad)
  sketch-geometry (1):
    g0: Circle CenterX=18 CenterY=0 CenterZ=0 NormalX=0 NormalY=0 NormalZ=1 AngleXU=0 Radius=5
  constraints (2):
    c: Diameter(g0) = 10
    c: Coincident(g0,g-3)
FEATURE [PartDesign::Pocket] Pocket098
  BaseFeature = -> Pocket097
  Direction = (0,0,1)
  Length = 25
  Length2 = 5
  Placement = pos=(0,0,0) rot=(1,0,0;1.5708rad)
  Profile = -> Sketch239
  ReferenceAxis = -> Sketch239 [N_Axis]
  Suppressed = false
  Type = 0
FEATURE [PartDesign::Fillet] Fillet001
  Base = -> Pocket098 [Edge63,Edge36,Edge37]
  BaseFeature = -> Pocket098
  Placement = pos=(0,0,0) rot=(1,0,0;1.5708rad)
  Radius = 0.81
  SupportTransform = false
  Suppressed = false
  UseAllEdges = false
FEATURE [PartDesign::Body] Body082  label="support_rail_haut"
  AllowCompound = false
  Group = -> [Sketch235,Sketch236,Pad114,Sketch237,Pad115,Mirrored010,Pocket096,Sketch238,Pocket097,Sketch239,Pocket098,Fillet001]
  Origin = -> Origin281
  Placement = pos=(2e-16,0,214.5) rot=(-0.707107,0,-0.707107;3.14159rad)
  Tip = -> Fillet001
COMPONENT P3 — recipe-attached ("pince_capot001", modeled in this document).
Construction recipe (the document's own serialized feature program — sketch geometry with constraints, then the solid features built on it; lengths are millimeters unless a unit is written):

FEATURE [Sketcher::SketchObject] Sketch242
  ArcFitTolerance = 0
  AttachmentSupport = -> [XY_Plane281]
  FullyConstrained = true
  MakeInternals = false
  MapMode = 2
  sketch-geometry (31):
    g0: LineSegment StartX=0 StartY=50 StartZ=0 EndX=100 EndY=50 EndZ=0
    g1: LineSegment StartX=100 StartY=50 StartZ=0 EndX=100 EndY=48 EndZ=0
    g2: LineSegment StartX=100 StartY=0 StartZ=0 EndX=0 EndY=0 EndZ=0
    g3: LineSegment StartX=0 StartY=0 StartZ=0 EndX=0 EndY=2 EndZ=0
    g4: Circle CenterX=50 CenterY=25 CenterZ=0 NormalX=0 NormalY=0 NormalZ=1 AngleXU=0 Radius=14
    g5: LineSegment [constr] StartX=0 StartY=50 StartZ=0 EndX=100 EndY=0 EndZ=0
    g6: LineSegment [constr] StartX=0 StartY=0 StartZ=0 EndX=100 EndY=50 EndZ=0
    g7: LineSegment [constr] StartX=0 StartY=25 StartZ=0 EndX=100 EndY=25 EndZ=0
    g8: LineSegment [constr] StartX=50 StartY=50 StartZ=0 EndX=50 EndY=0 EndZ=0
    g9: LineSegment [constr] StartX=3.5 StartY=33.25 StartZ=0 EndX=96.5 EndY=33.25 EndZ=0
    g10: LineSegment [constr] StartX=96.5 StartY=33.25 StartZ=0 EndX=96.5 EndY=16.75 EndZ=0
    g11: LineSegment [constr] StartX=96.5 StartY=16.75 StartZ=0 EndX=3.5 EndY=16.75 EndZ=0
    g12: LineSegment [constr] StartX=3.5 StartY=16.75 StartZ=0 EndX=3.5 EndY=33.25 EndZ=0
    g13: Circle CenterX=96.5 CenterY=33.25 CenterZ=0 NormalX=0 NormalY=0 NormalZ=1 AngleXU=0 Radius=1.65
    g14: Circle CenterX=3.5 CenterY=33.25 CenterZ=0 NormalX=0 NormalY=0 NormalZ=1 AngleXU=0 Radius=1.65
    g15: Circle CenterX=3.5 CenterY=16.75 CenterZ=0 NormalX=0 NormalY=0 NormalZ=1 AngleXU=0 Radius=1.65
    g16: Circle CenterX=96.5 CenterY=16.75 CenterZ=0 NormalX=0 NormalY=0 NormalZ=1 AngleXU=0 Radius=1.65
    g17: LineSegment StartX=0 StartY=2 StartZ=0 EndX=30 EndY=2 EndZ=0
    g18: LineSegment StartX=30 StartY=2 StartZ=0 EndX=30 EndY=7.5 EndZ=0
    g19: LineSegment StartX=30 StartY=7.5 StartZ=0 EndX=2.5 EndY=7.5 EndZ=0
    g20: LineSegment StartX=0 StartY=10 StartZ=0 EndX=0 EndY=50 EndZ=0
    g21: LineSegment StartX=100 StartY=48 StartZ=0 EndX=67.5 EndY=48 EndZ=0
    g22: LineSegment StartX=67.5 StartY=48 StartZ=0 EndX=67.5 EndY=42.5 EndZ=0
    g23: LineSegment StartX=67.5 StartY=42.5 StartZ=0 EndX=97.5 EndY=42.5 EndZ=0
    g24: LineSegment StartX=100 StartY=40 StartZ=0 EndX=100 EndY=0 EndZ=0
    g25: ArcOfCircle [constr] CenterX=97.5 CenterY=40 CenterZ=0 NormalX=0 NormalY=0 NormalZ=1 AngleXU=0 Radius=2.5 StartAngle=0 EndAngle=1.5708
    g26: GeomPoint [constr] X=100 Y=42.5 Z=0
    g27: LineSegment StartX=100 StartY=40 StartZ=0 EndX=97.5 EndY=42.5 EndZ=0
    g28: ArcOfCircle [constr] CenterX=2.5 CenterY=10 CenterZ=0 NormalX=0 NormalY=0 NormalZ=1 AngleXU=0 Radius=2.5 StartAngle=3.14159 EndAngle=4.71239
    g29: GeomPoint [constr] X=0 Y=7.5 Z=0
    g30: LineSegment StartX=0 StartY=10 StartZ=0 EndX=2.5 EndY=7.5 EndZ=0
  constraints (78):
    c: Coincident(g0,g1)
    c: Coincident(g24,g2)
    c: Coincident(g2,g3)
    c: Coincident(g20,g0)
    c: Horizontal(g0)
    c: Horizontal(g2)
    c: Vertical(g1)
    c: Vertical(g3)
    c: Coincident(g2,g-1)
    c: Coincident(g5,g0)
    c: Coincident(g2,g6)
    c: Coincident(g0,g6)
    c: Coincident(g24,g5)
    c: PointOnObject(g4,g6)
    c: PointOnObject(g4,g5)
    c: Diameter(g4) = 28
    c: DistanceY(g3,g20) = 50
    c: DistanceX(g2,g2) = 100
    c: PointOnObject(g8,g0)
    c: PointOnObject(g7,g24)
    c: PointOnObject(g7,g20)
    c: PointOnObject(g8,g2)
    c: Symmetric(g0,g0,g8)
    c: Symmetric(g0,g2,g7)
    c: Coincident(g9,g10)
    c: Coincident(g10,g11)
    c: Coincident(g11,g12)
    c: Coincident(g12,g9)
    c: Horizontal(g11)
    c: Vertical(g12)
    c: Symmetric(g9,g10,g7)
    c: Symmetric(g9,g9,g8)
    c: Distance(g12) = 16.5
    c: DistanceX(g0,g9) = 3.5
    c: Coincident(g16,g10)
    c: Coincident(g13,g9)
    c: Coincident(g9,g14)
    c: Coincident(g11,g15)
    c: Equal(g14,g15)
    c: Equal(g14,g13)
    c: Equal(g14,g16)
    c: Diameter(g14) = 3.3
    c: Coincident(g17,g18)
    c: Coincident(g18,g19)
    c: Horizontal(g17)
    c: Horizontal(g19)
    c: Vertical(g18)
    c: Vertical(g20)
    c: DistanceX(g29,g19) = 30
    c: Coincident(g21,g22)
    c: Coincident(g22,g23)
    c: Horizontal(g21)
    c: Horizontal(g23)
    c: Vertical(g22)
    c: Vertical(g24)
    c: Equal(g18,g22)
    c: PointOnObject(g26,g23)
    c: PointOnObject(g26,g24)
    c: Tangent(g23,g25) = 1.5708
    c: Tangent(g24,g25) = 1.5708
    c: Coincident(g27,g23)
    c: Coincident(g27,g24)
    c: PointOnObject(g29,g20)
    c: PointOnObject(g29,g19)
    c: Tangent(g20,g28) = 1.5708
    c: Tangent(g19,g28) = 1.5708
    c: Coincident(g30,g20)
    c: Coincident(g30,g19)
    c: Equal(g1,g3)
    c: Equal(g23,g17)
    c: Coincident(g3,g17)
    c: DistanceY(g3,g3) = 2
    c: Coincident(g1,g21)
    c: Vertical(g1,g24)
    c: Vertical(g29,g3)
    c: DistanceY(g18,g18) = 5.5
    c: Radius(g28) = 2.5
    c: Equal(g25,g28)
FEATURE [PartDesign::Pad] Pad118
  AlongSketchNormal = false
  Direction = (0,0,1)
  Length = 4
  Length2 = 100
  Profile = -> Sketch242
  ReferenceAxis = -> Sketch242 [N_Axis]
  Suppressed = false
  Type = 0
FEATURE [Sketcher::SketchObject] Sketch243
  ArcFitTolerance = 1e-06
  AttachmentOffset = pos=(0,0,4) rot=(0,0,1;0rad)
  AttachmentSupport = -> [XY_Plane281]
  ExternalGeometry = -> [Pad118]
  FullyConstrained = true
  MakeInternals = false
  MapMode = 5
  Placement = pos=(0,0,4) rot=(0,0,1;0rad)
  sketch-geometry (4):
    g0: Circle CenterX=3.5 CenterY=33.25 CenterZ=0 NormalX=0 NormalY=0 NormalZ=1 AngleXU=0 Radius=3.25
    g1: Circle CenterX=3.5 CenterY=16.75 CenterZ=0 NormalX=0 NormalY=0 NormalZ=1 AngleXU=0 Radius=3.25
    g2: Circle CenterX=96.5 CenterY=33.25 CenterZ=0 NormalX=0 NormalY=0 NormalZ=1 AngleXU=0 Radius=3.25
    g3: Circle CenterX=96.5 CenterY=16.75 CenterZ=0 NormalX=0 NormalY=0 NormalZ=1 AngleXU=0 Radius=3.25
  constraints (10):
    c: Coincident(g0,g-3)
    c: Coincident(g1,g-4)
    c: Equal(g0,g1)
    c: Equal(g1,g2)
    c: Equal(g2,g3)
    c: Diameter(g0) = 6.5
    c: Horizontal(g3,g1)
    c: Horizontal(g2,g0)
    c: Vertical(g2,g3)
    c: DistanceX(g1,g3) = 93
FEATURE [PartDesign::Pocket] Pocket099
  BaseFeature = -> Pad118
  Direction = (0,0,-1)
  Length = 2
  Length2 = 5
  Profile = -> Sketch243
  ReferenceAxis = -> Sketch243 [N_Axis]
  Refine = true
  Suppressed = false
  Type = 0
FEATURE [PartDesign::Body] Body083  label="pince_capot001"
  AllowCompound = false
  Group = -> [Sketch242,Pad118,Sketch243,Pocket099]
  Origin = -> Origin284
  Placement = pos=(-25,-5,28) rot=(0,0,1;0rad)
  Tip = -> Pocket099
COMPONENT P4 — recipe-attached ("pince_cremaillere_bras002", modeled in this document).
Construction recipe (the document's own serialized feature program — sketch geometry with constraints, then the solid features built on it; lengths are millimeters unless a unit is written):

FEATURE [PartDesign::FeatureBase] BaseFeature002
  BaseFeature = -> InvoluteRack001
  Suppressed = false
FEATURE [Sketcher::SketchObject] Sketch244
  ArcFitTolerance = 1e-06
  AttachmentSupport = -> [BaseFeature002]
  FullyConstrained = true
  MakeInternals = false
  MapMode = 5
  Placement = pos=(0,92.677,0) rot=(0,0.707107,0.707107;3.14159rad)
  sketch-geometry (4):
    g0: LineSegment StartX=-29.25 StartY=0 StartZ=0 EndX=10.75 EndY=0 EndZ=0
    g1: LineSegment StartX=10.75 StartY=0 StartZ=0 EndX=10.75 EndY=40 EndZ=0
    g2: LineSegment StartX=10.75 StartY=40 StartZ=0 EndX=-29.25 EndY=40 EndZ=0
    g3: LineSegment StartX=-29.25 StartY=40 StartZ=0 EndX=-29.25 EndY=0 EndZ=0
  constraints (12):
    c: Coincident(g0,g1)
    c: Coincident(g1,g2)
    c: Coincident(g2,g3)
    c: Coincident(g3,g0)
    c: Horizontal(g0)
    c: Horizontal(g2)
    c: Vertical(g1)
    c: Vertical(g3)
    c: DistanceY(g3,g3) = 40
    c: DistanceX(g2,g2) = 40
    c: PointOnObject(g0,g-1)
    c: DistanceX(g-1,g0) = 10.75
FEATURE [PartDesign::Pad] Pad119
  BaseFeature = -> BaseFeature002
  Direction = (0,1,-2e-16)
  Length = 5
  Length2 = 10
  Profile = -> Sketch244
  ReferenceAxis = -> Sketch244 [N_Axis]
  Refine = true
  Suppressed = false
  Type = 0
FEATURE [Sketcher::SketchObject] Sketch262
  ArcFitTolerance = 1e-06
  AttachmentOffset = pos=(0,0,-10.75) rot=(0,0,1;0rad)
  AttachmentSupport = -> [YZ_Plane282]
  ExternalGeometry = -> [Pad119]
  FullyConstrained = true
  MakeInternals = false
  MapMode = 5
  Placement = pos=(-10.75,0,0) rot=(0.57735,0.57735,0.57735;2.0944rad)
  sketch-geometry (3):
    g0: LineSegment StartX=67.677 StartY=3 StartZ=0 EndX=92.677 EndY=9 EndZ=0
    g1: LineSegment StartX=67.677 StartY=3 StartZ=0 EndX=92.677 EndY=3 EndZ=0
    g2: LineSegment StartX=92.677 StartY=9 StartZ=0 EndX=92.677 EndY=3 EndZ=0
  constraints (8):
    c: PointOnObject(g0,g-4)
    c: Coincident(g1,g0)
    c: Coincident(g1,g-4)
    c: Coincident(g2,g0)
    c: Coincident(g2,g1)
    c: DistanceX(g1,g1) = 25
    c: Vertical(g2)
    c: DistanceY(g2,g2) = 6
FEATURE [PartDesign::Pad] Pad124
  BaseFeature = -> Pad119
  Direction = (1,0,0)
  Length = 5
  Length2 = 10
  Profile = -> Sketch262
  ReferenceAxis = -> Sketch262 [N_Axis]
  Suppressed = false
  Type = 0
FEATURE [PartDesign::Body] Body084  label="pince_cremaillere_bras002"
  AllowCompound = false
  BaseFeature = -> InvoluteRack001
  Group = -> [BaseFeature002,Sketch244,Pad119,Sketch262,Pad124]
  Origin = -> Origin285
  Placement = pos=(-18.1714,32.25,24) rot=(0,0,-1;1.5708rad)
  Tip = -> Pad124
COMPONENT P5 — recipe-attached ("pince_support_servo001", modeled in this document).
Construction recipe (the document's own serialized feature program — sketch geometry with constraints, then the solid features built on it; lengths are millimeters unless a unit is written):

FEATURE [Sketcher::SketchObject] Sketch245
  ArcFitTolerance = 0
  AttachmentOffset = pos=(0,0,-2) rot=(0,0,1;0rad)
  AttachmentSupport = -> [XY_Plane283]
  FullyConstrained = true
  MakeInternals = false
  MapMode = 2
  Placement = pos=(0,0,-2) rot=(0,0,1;0rad)
  sketch-geometry (18):
    g0: LineSegment StartX=14.5 StartY=50 StartZ=0 EndX=35.5 EndY=50 EndZ=0
    g1: LineSegment StartX=35.5 StartY=50 StartZ=0 EndX=35.5 EndY=9 EndZ=0
    g2: LineSegment StartX=35.5 StartY=9 StartZ=0 EndX=14.5 EndY=9 EndZ=0
    g3: LineSegment StartX=14.5 StartY=9 StartZ=0 EndX=14.5 EndY=50 EndZ=0
    g4: LineSegment StartX=0 StartY=59 StartZ=0 EndX=50 EndY=59 EndZ=0
    g5: LineSegment StartX=50 StartY=59 StartZ=0 EndX=50 EndY=0 EndZ=0
    g6: LineSegment StartX=50 StartY=0 StartZ=0 EndX=0 EndY=0 EndZ=0
    g7: LineSegment StartX=0 StartY=0 StartZ=0 EndX=0 EndY=59 EndZ=0
    g8: Circle CenterX=19 CenterY=54.5 CenterZ=0 NormalX=0 NormalY=0 NormalZ=1 AngleXU=0 Radius=1.65
    g9: Circle CenterX=31 CenterY=54.5 CenterZ=0 NormalX=0 NormalY=0 NormalZ=1 AngleXU=0 Radius=1.65
    g10: Circle CenterX=19 CenterY=4.5 CenterZ=0 NormalX=0 NormalY=0 NormalZ=1 AngleXU=0 Radius=1.65
    g11: Circle CenterX=31 CenterY=4.5 CenterZ=0 NormalX=0 NormalY=0 NormalZ=1 AngleXU=0 Radius=1.65
    g12: LineSegment [constr] StartX=19 StartY=54.5 StartZ=0 EndX=31 EndY=54.5 EndZ=0
    g13: LineSegment [constr] StartX=31 StartY=54.5 StartZ=0 EndX=31 EndY=4.5 EndZ=0
    g14: LineSegment [constr] StartX=31 StartY=4.5 StartZ=0 EndX=19 EndY=4.5 EndZ=0
    g15: LineSegment [constr] StartX=19 StartY=4.5 StartZ=0 EndX=19 EndY=54.5 EndZ=0
    g16: LineSegment [constr] StartX=14.5 StartY=29.5 StartZ=0 EndX=35.5 EndY=29.5 EndZ=0
    g17: LineSegment [constr] StartX=25 StartY=50 StartZ=0 EndX=25 EndY=9 EndZ=0
  constraints (46):
    c: Coincident(g0,g1)
    c: Coincident(g1,g2)
    c: Coincident(g2,g3)
    c: Coincident(g3,g0)
    c: Horizontal(g0)
    c: Horizontal(g2)
    c: Vertical(g1)
    c: Vertical(g3)
    c: Coincident(g4,g5)
    c: Coincident(g5,g6)
    c: Coincident(g6,g7)
    c: Coincident(g7,g4)
    c: Horizontal(g6)
    c: Vertical(g5)
    c: Coincident(g12,g13)
    c: Coincident(g13,g14)
    c: Coincident(g14,g15)
    c: Coincident(g15,g12)
    c: Horizontal(g14)
    c: Vertical(g15)
    c: Coincident(g10,g14)
    c: Coincident(g11,g13)
    c: Coincident(g8,g12)
    c: Coincident(g9,g12)
    c: PointOnObject(g17,g0)
    c: PointOnObject(g17,g2)
    c: PointOnObject(g16,g3)
    c: PointOnObject(g16,g1)
    c: Symmetric(g0,g0,g17)
    c: Symmetric(g2,g0,g16)
    c: Symmetric(g9,g8,g17)
    c: DistanceX(g2,g2) = 21
    c: DistanceY(g3,g3) = 41
    c: DistanceX(g14,g14) = 12
    c: DistanceY(g13,g13) = 50
    c: Equal(g9,g8)
    c: Equal(g9,g11)
    c: Equal(g9,g10)
    c: Diameter(g9) = 3.3
    c: Symmetric(g9,g11,g16)
    c: Coincident(g-1,g6)
    c: Symmetric(g4,g4,g17)
    c: DistanceX(g6,g2) = 14.5
    c: Vertical(g7)
    c: DistanceY(g5,g5) = 59
    c: DistanceY(g-1,g2) = 9
FEATURE [PartDesign::Pad] Pad120
  AlongSketchNormal = false
  Direction = (0,0,1)
  Length = 4
  Length2 = 100
  Profile = -> Sketch245
  ReferenceAxis = -> Sketch245 [N_Axis]
  Suppressed = false
  Type = 0
FEATURE [Sketcher::SketchObject] Sketch246
  ArcFitTolerance = 0
  AttachmentSupport = -> [Pad120]
  ExternalGeometry = -> [Pad120]
  FullyConstrained = true
  MakeInternals = false
  MapMode = 5
  Placement = pos=(0,0,2) rot=(0,0,1;0rad)
  sketch-geometry (10):
    g0: LineSegment StartX=0 StartY=40 StartZ=0 EndX=8 EndY=40 EndZ=0
    g1: LineSegment StartX=8 StartY=40 StartZ=0 EndX=8 EndY=0 EndZ=0
    g2: LineSegment StartX=8 StartY=0 StartZ=0 EndX=0 EndY=0 EndZ=0
    g3: LineSegment StartX=0 StartY=0 StartZ=0 EndX=0 EndY=40 EndZ=0
    g4: LineSegment StartX=42 StartY=40 StartZ=0 EndX=50 EndY=40 EndZ=0
    g5: LineSegment StartX=50 StartY=40 StartZ=0 EndX=50 EndY=0 EndZ=0
    g6: LineSegment StartX=50 StartY=0 StartZ=0 EndX=42 EndY=0 EndZ=0
    g7: LineSegment StartX=42 StartY=0 StartZ=0 EndX=42 EndY=40 EndZ=0
    g8: LineSegment [constr] StartX=25 StartY=59 StartZ=0 EndX=25 EndY=0 EndZ=0
    g9: LineSegment [constr] StartX=0 StartY=20 StartZ=0 EndX=50 EndY=20 EndZ=0
  constraints (28):
    c: Coincident(g0,g1)
    c: Coincident(g1,g2)
    c: Coincident(g2,g3)
    c: Coincident(g3,g0)
    c: Horizontal(g0)
    c: Horizontal(g2)
    c: Vertical(g3)
    c: Coincident(g4,g5)
    c: Coincident(g5,g6)
    c: Coincident(g6,g7)
    c: Coincident(g7,g4)
    c: Horizontal(g4)
    c: Horizontal(g6)
    c: Vertical(g5)
    c: PointOnObject(g4,g-4)
    c: PointOnObject(g8,g-5)
    c: PointOnObject(g8,g-6)
    c: Symmetric(g-5,g-5,g8)
    c: Symmetric(g0,g4,g8)
    c: DistanceX(g0,g0) = 8
    c: Vertical(g1)
    c: PointOnObject(g9,g3)
    c: PointOnObject(g9,g5)
    c: Symmetric(g0,g1,g9)
    c: Vertical(g7)
    c: PointOnObject(g5,g-1)
    c: DistanceY(g3,g3) = 40
    c: Coincident(g2,g-1)
FEATURE [PartDesign::Pad] Pad121
  AlongSketchNormal = false
  BaseFeature = -> Pad120
  Direction = (0,0,1)
  Length = 18
  Length2 = 100
  Profile = -> Sketch246
  Suppressed = false
  Type = 0
FEATURE [Sketcher::SketchObject] Sketch247
  ArcFitTolerance = 0
  AttachmentSupport = -> [Pad121]
  ExternalGeometry = -> [Pad121]
  FullyConstrained = true
  MakeInternals = false
  MapMode = 5
  Placement = pos=(0,0,20) rot=(0,0,1;0rad)
  sketch-geometry (7):
    g0: LineSegment [constr] StartX=25 StartY=40 StartZ=0 EndX=25 EndY=0 EndZ=0
    g1: LineSegment [constr] StartX=0 StartY=20 StartZ=0 EndX=50 EndY=20 EndZ=0
    g2: Circle CenterX=4 CenterY=36 CenterZ=0 NormalX=0 NormalY=0 NormalZ=1 AngleXU=0 Radius=1.75
    g3: Circle CenterX=46 CenterY=36 CenterZ=0 NormalX=0 NormalY=0 NormalZ=1 AngleXU=0 Radius=1.75
    g4: Circle CenterX=4 CenterY=4 CenterZ=0 NormalX=0 NormalY=0 NormalZ=1 AngleXU=0 Radius=1.75
    g5: Circle CenterX=46 CenterY=4 CenterZ=0 NormalX=0 NormalY=0 NormalZ=1 AngleXU=0 Radius=1.75
    g6: LineSegment [constr] StartX=4 StartY=36 StartZ=0 EndX=4 EndY=4 EndZ=0
  constraints (17):
    c: PointOnObject(g0,g-4)
    c: PointOnObject(g0,g-5)
    c: PointOnObject(g1,g-7)
    c: PointOnObject(g1,g-8)
    c: Symmetric(g-3,g-4,g0)
    c: Symmetric(g-5,g-4,g1)
    c: Symmetric(g4,g2,g1)
    c: Symmetric(g3,g2,g0)
    c: Symmetric(g5,g3,g1)
    c: Equal(g2,g4)
    c: Equal(g2,g3)
    c: Equal(g2,g5)
    c: Radius(g2) = 1.75
    c: Coincident(g6,g4)
    c: Coincident(g6,g2)
    c: Symmetric(g-7,g-5,g6)
    c: DistanceY(g-5,g4) = 4
FEATURE [PartDesign::Pocket] Pocket100
  BaseFeature = -> Pad121
  Direction = (0,0,-1)
  Length = 5
  Length2 = 100
  Profile = -> Sketch247
  Suppressed = false
  Type = 1
FEATURE [Sketcher::SketchObject] Sketch248
  ArcFitTolerance = 0
  AttachmentSupport = -> [Pocket100]
  ExternalGeometry = -> [Pocket100]
  FullyConstrained = true
  MakeInternals = false
  MapMode = 5
  Placement = pos=(50,0,0) rot=(0.57735,0.57735,0.57735;2.0944rad)
  sketch-geometry (7):
    g0: LineSegment [constr] StartX=0 StartY=20 StartZ=0 EndX=40 EndY=0 EndZ=0
    g1: LineSegment [constr] StartX=0 StartY=0 StartZ=0 EndX=40 EndY=20 EndZ=0
    g2: Circle CenterX=12 CenterY=17 CenterZ=0 NormalX=0 NormalY=0 NormalZ=1 AngleXU=0 Radius=1.75
    g3: Circle CenterX=12 CenterY=3 CenterZ=0 NormalX=0 NormalY=0 NormalZ=1 AngleXU=0 Radius=1.75
    g4: Circle CenterX=28 CenterY=3 CenterZ=0 NormalX=0 NormalY=0 NormalZ=1 AngleXU=0 Radius=1.75
    g5: Circle CenterX=28 CenterY=17 CenterZ=0 NormalX=0 NormalY=0 NormalZ=1 AngleXU=0 Radius=1.75
    g6: GeomPoint X=20 Y=10 Z=0
  constraints (19):
    c: Equal(g3,g2)
    c: Equal(g3,g5)
    c: Equal(g3,g4)
    c: Coincident(g0,g-5)
    c: Coincident(g1,g-4)
    c: DistanceX(g-3,g-3) = 40
    c: Horizontal(g2,g5)
    c: Horizontal(g3,g4)
    c: Diameter(g3) = 3.5
    c: Vertical(g3,g2)
    c: Vertical(g5,g4)
    c: PointOnObject(g6,g0)
    c: PointOnObject(g6,g1)
    c: DistanceX(g2,g6) = 8
    c: DistanceY(g6,g2) = 7
    c: Symmetric(g2,g4,g6)
    c: Coincident(g1,g-1)
    c: PointOnObject(g0,g-1)
    c: Vertical(g-4,g0)
FEATURE [PartDesign::Pocket] Pocket101
  BaseFeature = -> Pocket100
  Direction = (-1,0,0)
  Length = 5
  Length2 = 100
  Profile = -> Sketch248
  ReferenceAxis = -> Sketch248 [N_Axis]
  Suppressed = false
  Type = 1
FEATURE [Sketcher::SketchObject] Sketch249
  ArcFitTolerance = 1e-06
  AttachmentSupport = -> [Pocket101]
  ExternalGeometry = -> [Pocket101]
  FullyConstrained = true
  MakeInternals = false
  MapMode = 5
  Placement = pos=(50,0,0) rot=(0.57735,0.57735,0.57735;2.0944rad)
  sketch-geometry (4):
    g0: Circle CenterX=12 CenterY=17 CenterZ=0 NormalX=0 NormalY=0 NormalZ=1 AngleXU=0 Radius=2.125
    g1: Circle CenterX=28 CenterY=17 CenterZ=0 NormalX=0 NormalY=0 NormalZ=1 AngleXU=0 Radius=2.125
    g2: Circle CenterX=28 CenterY=3 CenterZ=0 NormalX=0 NormalY=0 NormalZ=1 AngleXU=0 Radius=2.125
    g3: Circle CenterX=12 CenterY=3 CenterZ=0 NormalX=0 NormalY=0 NormalZ=1 AngleXU=0 Radius=2.125
  constraints (8):
    c: Equal(g0,g1)
    c: Equal(g1,g3)
    c: Equal(g3,g2)
    c: Diameter(g0) = 4.25
    c: Coincident(g0,g-3)
    c: Coincident(g-4,g1)
    c: Coincident(g-5,g2)
    c: Coincident(g-6,g3)
FEATURE [PartDesign::Pocket] Pocket102
  BaseFeature = -> Pocket101
  Direction = (-1,0,0)
  Length = 1.5
  Length2 = 5
  Profile = -> Sketch249
  ReferenceAxis = -> Sketch249 [N_Axis]
  Refine = true
  Suppressed = false
  Type = 0
FEATURE [Sketcher::SketchObject] Sketch250
  ArcFitTolerance = 1e-06
  AttachmentSupport = -> [Pocket102]
  ExternalGeometry = -> [Pocket102]
  FullyConstrained = true
  MakeInternals = false
  MapMode = 5
  Placement = pos=(0,0,0) rot=(0.57735,-0.57735,-0.57735;2.0944rad)
  sketch-geometry (4):
    g0: Circle CenterX=-28 CenterY=17 CenterZ=0 NormalX=0 NormalY=0 NormalZ=1 AngleXU=0 Radius=2.1
    g1: Circle CenterX=-12 CenterY=17 CenterZ=0 NormalX=0 NormalY=0 NormalZ=1 AngleXU=0 Radius=2.1
    g2: Circle CenterX=-12 CenterY=3 CenterZ=0 NormalX=0 NormalY=0 NormalZ=1 AngleXU=0 Radius=2.1
    g3: Circle CenterX=-28 CenterY=3 CenterZ=0 NormalX=0 NormalY=0 NormalZ=1 AngleXU=0 Radius=2.1
  constraints (8):
    c: Equal(g0,g1)
    c: Equal(g1,g3)
    c: Equal(g3,g2)
    c: Diameter(g0) = 4.2
    c: Coincident(g0,g-3)
    c: Coincident(g-4,g1)
    c: Coincident(g-5,g2)
    c: Coincident(g3,g-6)
FEATURE [PartDesign::Pocket] Pocket103
  BaseFeature = -> Pocket102
  Direction = (1,0,0)
  Length = 1.5
  Length2 = 5
  Profile = -> Sketch250
  ReferenceAxis = -> Sketch250 [N_Axis]
  Refine = true
  Suppressed = false
  Type = 0
FEATURE [Sketcher::SketchObject] Sketch251
  ArcFitTolerance = 1e-06
  AttachmentSupport = -> [Pocket103]
  ExternalGeometry = -> [Pocket103]
  FullyConstrained = true
  MakeInternals = false
  MapMode = 5
  Placement = pos=(0,0,20) rot=(0,0,1;0rad)
  sketch-geometry (4):
    g0: Circle CenterX=4 CenterY=36 CenterZ=0 NormalX=0 NormalY=0 NormalZ=1 AngleXU=0 Radius=2.1
    g1: Circle CenterX=46 CenterY=36 CenterZ=0 NormalX=0 NormalY=0 NormalZ=1 AngleXU=0 Radius=2.1
    g2: Circle CenterX=4 CenterY=4 CenterZ=0 NormalX=0 NormalY=0 NormalZ=1 AngleXU=0 Radius=2.1
    g3: Circle CenterX=46 CenterY=4 CenterZ=0 NormalX=0 NormalY=0 NormalZ=1 AngleXU=0 Radius=2.1
  constraints (8):
    c: Coincident(g0,g-3)
    c: Coincident(g1,g-6)
    c: Coincident(g2,g-4)
    c: Coincident(g3,g-5)
    c: Equal(g0,g2)
    c: Equal(g2,g1)
    c: Equal(g1,g3)
    c: Diameter(g0) = 4.2
FEATURE [PartDesign::Pocket] Pocket104
  BaseFeature = -> Pocket103
  Direction = (0,0,-1)
  Length = 1.5
  Length2 = 5
  Profile = -> Sketch251
  ReferenceAxis = -> Sketch251 [N_Axis]
  Refine = true
  Suppressed = false
  Type = 0
FEATURE [Sketcher::SketchObject] Sketch252
  ArcFitTolerance = 1e-06
  AttachmentSupport = -> [Pocket104]
  ExternalGeometry = -> [Pocket104]
  FullyConstrained = true
  MakeInternals = false
  MapMode = 5
  Placement = pos=(0,0,-2) rot=(1,0,0;3.14159rad)
  sketch-geometry (4):
    g0: Circle CenterX=4 CenterY=-4 CenterZ=0 NormalX=0 NormalY=0 NormalZ=1 AngleXU=0 Radius=2.1
    g1: Circle CenterX=46 CenterY=-4 CenterZ=0 NormalX=0 NormalY=0 NormalZ=1 AngleXU=0 Radius=2.1
    g2: Circle CenterX=46 CenterY=-36 CenterZ=0 NormalX=0 NormalY=0 NormalZ=1 AngleXU=0 Radius=2.1
    g3: Circle CenterX=4 CenterY=-36 CenterZ=0 NormalX=0 NormalY=0 NormalZ=1 AngleXU=0 Radius=2.1
  constraints (8):
    c: Coincident(g0,g-3)
    c: Coincident(g1,g-5)
    c: Coincident(g2,g-6)
    c: Coincident(g3,g-4)
    c: Equal(g0,g1)
    c: Equal(g1,g2)
    c: Equal(g2,g3)
    c: Diameter(g0) = 4.2
FEATURE [PartDesign::Pocket] Pocket105
  BaseFeature = -> Pocket104
  Direction = (0,0,1)
  Length = 1.5
  Length2 = 5
  Profile = -> Sketch252
  ReferenceAxis = -> Sketch252 [N_Axis]
  Refine = true
  Suppressed = false
  Type = 0
FEATURE [PartDesign::Body] Body085  label="pince_support_servo001"
  AllowCompound = false
  Group = -> [Sketch245,Pad120,Sketch246,Pad121,Sketch247,Pocket100,Sketch248,Pocket101,Sketch249,Pocket102,Sketch250,Pocket103,Sketch251,Pocket104,Sketch252,Pocket105]
  Origin = -> Origin286
  Tip = -> Pocket105
COMPONENT P6 — recipe-attached ("pince_cremaillere_pignon001", modeled in this document).
Construction recipe (the document's own serialized feature program — sketch geometry with constraints, then the solid features built on it; lengths are millimeters unless a unit is written):

FEATURE [PartDesign::FeatureBase] BaseFeature003
  BaseFeature = -> InvoluteGear001
  Suppressed = false
FEATURE [Sketcher::SketchObject] Sketch253
  ArcFitTolerance = 0
  FullyConstrained = true
  MakeInternals = false
  MapMode = 5
  Placement = pos=(0,0,5.5) rot=(0,0,1;0rad)
  sketch-geometry (8):
    g0: Circle [constr] CenterX=0 CenterY=0 CenterZ=0 NormalX=0 NormalY=0 NormalZ=1 AngleXU=0 Radius=7
    g1: Circle CenterX=0 CenterY=7 CenterZ=0 NormalX=0 NormalY=0 NormalZ=1 AngleXU=0 Radius=1.65
    g2: Circle CenterX=-7 CenterY=0 CenterZ=0 NormalX=0 NormalY=0 NormalZ=1 AngleXU=0 Radius=1.65
    g3: Circle CenterX=7 CenterY=0 CenterZ=0 NormalX=0 NormalY=0 NormalZ=1 AngleXU=0 Radius=1.65
    g4: Circle CenterX=0 CenterY=-7 CenterZ=0 NormalX=0 NormalY=0 NormalZ=1 AngleXU=0 Radius=1.65
    g5: Circle CenterX=0 CenterY=0 CenterZ=0 NormalX=0 NormalY=0 NormalZ=1 AngleXU=0 Radius=3
    g6: LineSegment [constr] StartX=-7 StartY=0 StartZ=0 EndX=7 EndY=0 EndZ=0
    g7: LineSegment [constr] StartX=0 StartY=7 StartZ=0 EndX=0 EndY=-7 EndZ=0
  constraints (20):
    c: Coincident(g5,g0)
    c: Coincident(g5,g-1)
    c: PointOnObject(g2,g0)
    c: PointOnObject(g1,g0)
    c: PointOnObject(g3,g0)
    c: PointOnObject(g4,g0)
    c: Coincident(g2,g6)
    c: Coincident(g1,g7)
    c: Coincident(g6,g3)
    c: Coincident(g7,g4)
    c: PointOnObject(g5,g7)
    c: PointOnObject(g5,g6)
    c: Perpendicular(g7,g6)
    c: Equal(g1,g3)
    c: Equal(g1,g2)
    c: Equal(g1,g4)
    c: Diameter(g1) = 3.3
    c: Diameter(g5) = 6
    c: Diameter(g0) = 14
    c: PointOnObject(g2,g-1)
FEATURE [PartDesign::Pocket] Pocket106
  BaseFeature = -> BaseFeature003
  Direction = (0,0,-1)
  Length = 5
  Length2 = 100
  Profile = -> Sketch253
  Suppressed = false
  Type = 1
FEATURE [Sketcher::SketchObject] Sketch254
  ArcFitTolerance = 0
  AttachmentSupport = -> [Pocket106]
  ExternalGeometry = -> [Pocket106]
  FullyConstrained = true
  MakeInternals = false
  MapMode = 5
  Placement = pos=(0,0,0) rot=(1,0,0;3.14159rad)
  sketch-geometry (4):
    g0: Circle CenterX=0 CenterY=-7 CenterZ=0 NormalX=0 NormalY=0 NormalZ=1 AngleXU=0 Radius=3.25
    g1: Circle CenterX=-7 CenterY=0 CenterZ=0 NormalX=0 NormalY=0 NormalZ=1 AngleXU=0 Radius=3.25
    g2: Circle CenterX=7 CenterY=0 CenterZ=0 NormalX=0 NormalY=0 NormalZ=1 AngleXU=0 Radius=3.25
    g3: Circle CenterX=0 CenterY=7 CenterZ=0 NormalX=0 NormalY=0 NormalZ=1 AngleXU=0 Radius=3.25
  constraints (8):
    c: Coincident(g1,g-5)
    c: Coincident(g0,g-3)
    c: Coincident(g2,g-4)
    c: Coincident(g3,g-6)
    c: Equal(g2,g0)
    c: Equal(g2,g1)
    c: Equal(g2,g3)
    c: Diameter(g2) = 6.5
FEATURE [PartDesign::Pocket] Pocket107
  BaseFeature = -> Pocket106
  Direction = (0,0,1)
  Length = 3.5
  Length2 = 100
  Profile = -> Sketch254
  Suppressed = false
  Type = 0
FEATURE [PartDesign::Body] Body086  label="pince_cremaillere_pignon001"
  AllowCompound = false
  BaseFeature = -> InvoluteGear001
  Group = -> [BaseFeature003,Sketch253,Pocket106,Sketch254,Pocket107]
  Origin = -> Origin287
  Placement = pos=(25,20,27.098) rot=(0.715163,-0.698958,0;3.14159rad)
  Tip = -> Pocket107
COMPONENT P7 — recipe-attached ("pince_support_cremaillere001", modeled in this document).
Construction recipe (the document's own serialized feature program — sketch geometry with constraints, then the solid features built on it; lengths are millimeters unless a unit is written):

FEATURE [Sketcher::SketchObject] Sketch255
  ArcFitTolerance = 0
  FullyConstrained = true
  MakeInternals = false
  MapMode = 2
  sketch-geometry (25):
    g0: LineSegment StartX=0 StartY=50 StartZ=0 EndX=100 EndY=50 EndZ=0
    g1: LineSegment StartX=100 StartY=50 StartZ=0 EndX=100 EndY=0 EndZ=0
    g2: LineSegment StartX=100 StartY=0 StartZ=0 EndX=0 EndY=0 EndZ=0
    g3: LineSegment StartX=0 StartY=0 StartZ=0 EndX=0 EndY=50 EndZ=0
    g4: Circle CenterX=50 CenterY=25 CenterZ=0 NormalX=0 NormalY=0 NormalZ=1 AngleXU=0 Radius=14
    g5: LineSegment [constr] StartX=0 StartY=50 StartZ=0 EndX=100 EndY=0 EndZ=0
    g6: LineSegment [constr] StartX=0 StartY=0 StartZ=0 EndX=100 EndY=50 EndZ=0
    g7: LineSegment [constr] StartX=29 StartY=41 StartZ=0 EndX=71 EndY=41 EndZ=0
    g8: LineSegment [constr] StartX=71 StartY=41 StartZ=0 EndX=71 EndY=9 EndZ=0
    g9: LineSegment [constr] StartX=71 StartY=9 StartZ=0 EndX=29 EndY=9 EndZ=0
    g10: LineSegment [constr] StartX=29 StartY=9 StartZ=0 EndX=29 EndY=41 EndZ=0
    g11: Circle CenterX=29 CenterY=41 CenterZ=0 NormalX=0 NormalY=0 NormalZ=1 AngleXU=0 Radius=1.75
    g12: Circle CenterX=71 CenterY=41 CenterZ=0 NormalX=0 NormalY=0 NormalZ=1 AngleXU=0 Radius=1.75
    g13: Circle CenterX=71 CenterY=9 CenterZ=0 NormalX=0 NormalY=0 NormalZ=1 AngleXU=0 Radius=1.75
    g14: Circle CenterX=29 CenterY=9 CenterZ=0 NormalX=0 NormalY=0 NormalZ=1 AngleXU=0 Radius=1.75
    g15: LineSegment [constr] StartX=0 StartY=25 StartZ=0 EndX=100 EndY=25 EndZ=0
    g16: LineSegment [constr] StartX=50 StartY=50 StartZ=0 EndX=50 EndY=0 EndZ=0
    g17: LineSegment [constr] StartX=3.5 StartY=33.25 StartZ=0 EndX=96.5 EndY=33.25 EndZ=0
    g18: LineSegment [constr] StartX=96.5 StartY=33.25 StartZ=0 EndX=96.5 EndY=16.75 EndZ=0
    g19: LineSegment [constr] StartX=96.5 StartY=16.75 StartZ=0 EndX=3.5 EndY=16.75 EndZ=0
    g20: LineSegment [constr] StartX=3.5 StartY=16.75 StartZ=0 EndX=3.5 EndY=33.25 EndZ=0
    g21: Circle CenterX=96.5 CenterY=33.25 CenterZ=0 NormalX=0 NormalY=0 NormalZ=1 AngleXU=0 Radius=1.65
    g22: Circle CenterX=3.5 CenterY=33.25 CenterZ=0 NormalX=0 NormalY=0 NormalZ=1 AngleXU=0 Radius=1.65
    g23: Circle CenterX=3.5 CenterY=16.75 CenterZ=0 NormalX=0 NormalY=0 NormalZ=1 AngleXU=0 Radius=1.65
    g24: Circle CenterX=96.5 CenterY=16.75 CenterZ=0 NormalX=0 NormalY=0 NormalZ=1 AngleXU=0 Radius=1.65
  constraints (60):
    c: Coincident(g0,g1)
    c: Coincident(g1,g2)
    c: Coincident(g2,g3)
    c: Coincident(g3,g0)
    c: Horizontal(g0)
    c: Horizontal(g2)
    c: Vertical(g1)
    c: Vertical(g3)
    c: Coincident(g2,g-1)
    c: Coincident(g5,g0)
    c: Coincident(g2,g6)
    c: Coincident(g0,g6)
    c: Coincident(g1,g5)
    c: PointOnObject(g4,g6)
    c: PointOnObject(g4,g5)
    c: Diameter(g4) = 28
    c: DistanceY(g3,g3) = 50
    c: DistanceX(g2,g2) = 100
    c: Coincident(g7,g8)
    c: Coincident(g8,g9)
    c: Coincident(g9,g10)
    c: Coincident(g10,g7)
    c: Horizontal(g7)
    c: Vertical(g10)
    c: Coincident(g11,g7)
    c: Coincident(g7,g12)
    c: Coincident(g9,g14)
    c: Coincident(g8,g13)
    c: Equal(g11,g12)
    c: Equal(g11,g14)
    c: Equal(g11,g13)
    c: Radius(g11) = 1.75
    c: DistanceY(g10,g10) = 32
    c: DistanceX(g7,g7) = 42
    c: PointOnObject(g16,g0)
    c: PointOnObject(g15,g1)
    c: PointOnObject(g15,g3)
    c: PointOnObject(g16,g2)
    c: Symmetric(g0,g0,g16)
    c: Symmetric(g0,g2,g15)
    c: Symmetric(g14,g13,g16)
    c: Symmetric(g12,g13,g15)
    c: Coincident(g17,g18)
    c: Coincident(g18,g19)
    c: Coincident(g19,g20)
    c: Coincident(g20,g17)
    c: Horizontal(g19)
    c: Vertical(g20)
    c: Symmetric(g17,g18,g15)
    c: Symmetric(g17,g17,g16)
    c: Distance(g20) = 16.5
    c: DistanceX(g0,g17) = 3.5
    c: Coincident(g24,g18)
    c: Coincident(g21,g17)
    c: Coincident(g17,g22)
    c: Coincident(g19,g23)
    c: Equal(g22,g23)
    c: Equal(g22,g21)
    c: Equal(g22,g24)
    c: Diameter(g22) = 3.3
FEATURE [PartDesign::Pad] Pad122
  AlongSketchNormal = false
  Direction = (0,0,1)
  Length = 8
  Length2 = 100
  Profile = -> Sketch255
  Suppressed = false
  Type = 0
FEATURE [Sketcher::SketchObject] Sketch256
  ArcFitTolerance = 0
  AttachmentSupport = -> [Pad122]
  ExternalGeometry = -> [Pad122]
  FullyConstrained = true
  MakeInternals = false
  MapMode = 5
  Placement = pos=(0,0,8) rot=(0,0,1;0rad)
  sketch-geometry (9):
    g0: LineSegment StartX=0 StartY=48 StartZ=0 EndX=100 EndY=48 EndZ=0
    g1: LineSegment StartX=100 StartY=48 StartZ=0 EndX=100 EndY=35.75 EndZ=0
    g2: LineSegment StartX=100 StartY=35.75 StartZ=0 EndX=0 EndY=35.75 EndZ=0
    g3: LineSegment StartX=0 StartY=35.75 StartZ=0 EndX=0 EndY=48 EndZ=0
    g4: LineSegment StartX=0 StartY=2 StartZ=0 EndX=100 EndY=2 EndZ=0
    g5: LineSegment StartX=100 StartY=2 StartZ=0 EndX=100 EndY=14.25 EndZ=0
    g6: LineSegment StartX=100 StartY=14.25 StartZ=0 EndX=0 EndY=14.25 EndZ=0
    g7: LineSegment StartX=0 StartY=14.25 StartZ=0 EndX=0 EndY=2 EndZ=0
    g8: Circle [constr] CenterX=50 CenterY=25 CenterZ=0 NormalX=0 NormalY=0 NormalZ=1 AngleXU=0 Radius=10.75
  constraints (26):
    c: Coincident(g0,g1)
    c: Coincident(g1,g2)
    c: Coincident(g2,g3)
    c: Coincident(g3,g0)
    c: Horizontal(g0)
    c: Horizontal(g2)
    c: Vertical(g1)
    c: Vertical(g3)
    c: Coincident(g4,g5)
    c: Coincident(g5,g6)
    c: Coincident(g6,g7)
    c: Coincident(g7,g4)
    c: Horizontal(g4)
    c: Horizontal(g6)
    c: Vertical(g5)
    c: Vertical(g7)
    c: PointOnObject(g6,g-6)
    c: PointOnObject(g2,g-6)
    c: PointOnObject(g1,g-5)
    c: PointOnObject(g5,g-5)
    c: Coincident(g8,g-7)
    c: Diameter(g8) = 21.5
    c: Tangent(g8,g2)
    c: Tangent(g6,g8)
    c: Equal(g7,g3)
    c: DistanceY(g0,g-6) = 2
FEATURE [PartDesign::Pocket] Pocket108
  BaseFeature = -> Pad122
  Direction = (0,0,-1)
  Length = 4
  Length2 = 100
  Profile = -> Sketch256
  Suppressed = false
  Type = 0
FEATURE [Sketcher::SketchObject] Sketch257
  ArcFitTolerance = 0
  AttachmentSupport = -> [Pocket108]
  ExternalGeometry = -> [Pocket108]
  FullyConstrained = true
  MakeInternals = false
  MapMode = 5
  Placement = pos=(0,0,8) rot=(0,0,1;0rad)
  sketch-geometry (10):
    g0: ArcOfCircle CenterX=11 CenterY=25 CenterZ=0 NormalX=0 NormalY=0 NormalZ=1 AngleXU=0 Radius=8 StartAngle=1.5708 EndAngle=4.71239
    g1: ArcOfCircle CenterX=26 CenterY=25 CenterZ=0 NormalX=0 NormalY=0 NormalZ=1 AngleXU=0 Radius=8 StartAngle=4.71239 EndAngle=7.85398
    g2: LineSegment StartX=11 StartY=17 StartZ=0 EndX=26 EndY=17 EndZ=0
    g3: LineSegment StartX=26 StartY=33 StartZ=0 EndX=11 EndY=33 EndZ=0
    g4: ArcOfCircle CenterX=74 CenterY=25 CenterZ=0 NormalX=0 NormalY=0 NormalZ=1 AngleXU=0 Radius=8 StartAngle=1.5708 EndAngle=4.71239
    g5: ArcOfCircle CenterX=89 CenterY=25 CenterZ=0 NormalX=0 NormalY=0 NormalZ=1 AngleXU=0 Radius=8 StartAngle=4.71239 EndAngle=7.85398
    g6: LineSegment StartX=74 StartY=17 StartZ=0 EndX=89 EndY=17 EndZ=0
    g7: LineSegment StartX=89 StartY=33 StartZ=0 EndX=74 EndY=33 EndZ=0
    g8: LineSegment [constr] StartX=50 StartY=50 StartZ=0 EndX=50 EndY=0 EndZ=0
    g9: LineSegment [constr] StartX=0 StartY=25 StartZ=0 EndX=100 EndY=25 EndZ=0
  constraints (26):
    c: Tangent(g0,g2) = -1.5708
    c: Tangent(g2,g1) = -1.5708
    c: Tangent(g1,g3) = -1.5708
    c: Tangent(g3,g0) = -1.5708
    c: Equal(g0,g1)
    c: Tangent(g4,g6) = -1.5708
    c: Tangent(g6,g5) = -1.5708
    c: Tangent(g5,g7) = -1.5708
    c: Tangent(g7,g4) = -1.5708
    c: Equal(g4,g5)
    c: PointOnObject(g-7,g9)
    c: PointOnObject(g-7,g8)
    c: PointOnObject(g8,g-6)
    c: PointOnObject(g8,g-5)
    c: PointOnObject(g9,g-3)
    c: PointOnObject(g9,g-4)
    c: Horizontal(g9)
    c: Vertical(g8)
    c: PointOnObject(g0,g9)
    c: PointOnObject(g1,g9)
    c: Symmetric(g1,g4,g8)
    c: Symmetric(g5,g0,g8)
    c: Equal(g1,g4)
    c: DistanceX(g-3,g0) = 11
    c: DistanceX(g1,g8) = 24
    c: DistanceY(g-7,g1) = 8
FEATURE [PartDesign::Pocket] Pocket109
  BaseFeature = -> Pocket108
  Direction = (0,0,-1)
  Length = 5
  Length2 = 100
  Profile = -> Sketch257
  Suppressed = false
  Type = 1
FEATURE [Sketcher::SketchObject] Sketch258
  ArcFitTolerance = 0
  AttachmentSupport = -> [Pocket109]
  ExternalGeometry = -> [Pocket109]
  FullyConstrained = true
  MakeInternals = false
  MapMode = 5
  Placement = pos=(0,0,4) rot=(0,0,1;0rad)
  sketch-geometry (4):
    g0: Circle CenterX=29 CenterY=41 CenterZ=0 NormalX=0 NormalY=0 NormalZ=1 AngleXU=0 Radius=3.5
    g1: Circle CenterX=71 CenterY=41 CenterZ=0 NormalX=0 NormalY=0 NormalZ=1 AngleXU=0 Radius=3.5
    g2: Circle CenterX=29 CenterY=9 CenterZ=0 NormalX=0 NormalY=0 NormalZ=1 AngleXU=0 Radius=3.5
    g3: Circle CenterX=71 CenterY=9 CenterZ=0 NormalX=0 NormalY=0 NormalZ=1 AngleXU=0 Radius=3.5
  constraints (8):
    c: Coincident(g-3,g0)
    c: Coincident(g1,g-4)
    c: Coincident(g2,g-5)
    c: Coincident(g3,g-6)
    c: Equal(g0,g1)
    c: Equal(g0,g2)
    c: Equal(g0,g3)
    c: Diameter(g0) = 7
FEATURE [PartDesign::Pocket] Pocket110
  BaseFeature = -> Pocket109
  Direction = (0,0,-1)
  Length = 2
  Length2 = 100
  Profile = -> Sketch258
  Suppressed = false
  Type = 0
FEATURE [PartDesign::Body] Body087  label="pince_support_cremaillere001"
  AllowCompound = false
  Group = -> [Sketch255,Pad122,Sketch256,Pocket108,Sketch257,Pocket109,Sketch258,Pocket110]
  Origin = -> Origin288
  Placement = pos=(-25,-5,20) rot=(0,0,1;0rad)
  Tip = -> Pocket110
COMPONENT P8 — recipe-attached ("mousse002", modeled in this document).
Construction recipe (the document's own serialized feature program — sketch geometry with constraints, then the solid features built on it; lengths are millimeters unless a unit is written):

FEATURE [Sketcher::SketchObject] Sketch259
  ArcFitTolerance = 1e-06
  AttachmentSupport = -> [XZ_Plane286]
  FullyConstrained = true
  MakeInternals = false
  MapMode = 5
  Placement = pos=(0,0,0) rot=(1,0,0;1.5708rad)
  sketch-geometry (4):
    g0: LineSegment StartX=-4.5 StartY=0 StartZ=0 EndX=4.5 EndY=0 EndZ=0
    g1: LineSegment StartX=4.5 StartY=0 StartZ=0 EndX=4.5 EndY=3 EndZ=0
    g2: LineSegment StartX=4.5 StartY=3 StartZ=0 EndX=-4.5 EndY=3 EndZ=0
    g3: LineSegment StartX=-4.5 StartY=3 StartZ=0 EndX=-4.5 EndY=0 EndZ=0
  constraints (11):
    c: Coincident(g0,g1)
    c: Coincident(g1,g2)
    c: Coincident(g2,g3)
    c: Coincident(g3,g0)
    c: Horizontal(g0)
    c: Vertical(g1)
    c: Vertical(g3)
    c: PointOnObject(g0,g-1)
    c: Symmetric(g1,g2,g-2)
    c: Distance(g2,g2) = 9
    c: DistanceY(g3,g3) = 3
FEATURE [PartDesign::Pad] Pad123
  Direction = (0,-1,2e-16)
  Length = 40
  Length2 = 10
  Midplane = true
  Placement = pos=(0,0,0) rot=(1,0,0;1.5708rad)
  Profile = -> Sketch259
  ReferenceAxis = -> Sketch259 [N_Axis]
  Suppressed = false
  Type = 0
FEATURE [PartDesign::Body] Body088  label="mousse002"
  AllowCompound = false
  Group = -> [Sketch259,Pad123]
  Origin = -> Origin289
  Placement = pos=(71.5056,23,59.5) rot=(0.707107,0,0.707107;3.14159rad)
  Tip = -> Pad123
COMPONENT P9 — recipe-attached ("support_rail_haut001", modeled in this document).
Construction recipe (the document's own serialized feature program — sketch geometry with constraints, then the solid features built on it; lengths are millimeters unless a unit is written):

FEATURE [Sketcher::SketchObject] Sketch263
  ArcFitTolerance = 1e-06
  AttachmentSupport = -> [YZ_Plane289]
  FullyConstrained = true
  MakeInternals = false
  MapMode = 5
  Placement = pos=(0,0,0) rot=(0.57735,0.57735,0.57735;2.0944rad)
  sketch-geometry (20):
    g0: LineSegment StartX=-16.6 StartY=41.5 StartZ=0 EndX=-16.6 EndY=39.5 EndZ=0
    g1: LineSegment StartX=-14.6 StartY=37.5 StartZ=0 EndX=-8.6 EndY=37.5 EndZ=0
    g2: LineSegment StartX=-6.6 StartY=35.5 StartZ=0 EndX=-6.6 EndY=-4.1 EndZ=0
    g3: LineSegment StartX=-4.6 StartY=-6.1 StartZ=0 EndX=0 EndY=-6.1 EndZ=0
    g4: LineSegment StartX=0 StartY=-6.1 StartZ=0 EndX=0 EndY=-0.1 EndZ=0
    g5: LineSegment StartX=0 StartY=-0.1 StartZ=0 EndX=-4.6 EndY=-0.1 EndZ=0
    g6: LineSegment StartX=-4.6 StartY=-0.1 StartZ=0 EndX=-4.6 EndY=6.6 EndZ=0
    g7: LineSegment StartX=-4.6 StartY=6.6 StartZ=0 EndX=0 EndY=6.6 EndZ=0
    g8: LineSegment StartX=0 StartY=6.6 StartZ=0 EndX=0 EndY=41.5 EndZ=0
    g9: LineSegment StartX=0 StartY=41.5 StartZ=0 EndX=-16.6 EndY=41.5 EndZ=0
    g10: ArcOfCircle CenterX=-8.6 CenterY=35.5 CenterZ=0 NormalX=0 NormalY=0 NormalZ=1 AngleXU=0 Radius=2 StartAngle=0 EndAngle=1.5708
    g11: GeomPoint [constr] X=-6.6 Y=37.5 Z=0
    g12: ArcOfCircle CenterX=-4.6 CenterY=-4.1 CenterZ=0 NormalX=0 NormalY=0 NormalZ=1 AngleXU=0 Radius=2 StartAngle=3.14159 EndAngle=4.71239
    g13: GeomPoint [constr] X=-6.6 Y=-6.1 Z=0
    g14: ArcOfCircle CenterX=-14.6 CenterY=39.5 CenterZ=0 NormalX=0 NormalY=0 NormalZ=1 AngleXU=0 Radius=2 StartAngle=3.14159 EndAngle=4.71239
    g15: GeomPoint [constr] X=-16.6 Y=37.5 Z=0
    g16: LineSegment [constr] StartX=-4.5 StartY=6.5 StartZ=0 EndX=-4.5 EndY=0 EndZ=0
    g17: LineSegment [constr] StartX=-4.5 StartY=0 StartZ=0 EndX=0 EndY=0 EndZ=0
    g18: LineSegment [constr] StartX=0 StartY=0 StartZ=0 EndX=0 EndY=6.5 EndZ=0
    g19: LineSegment [constr] StartX=0 StartY=6.5 StartZ=0 EndX=-4.5 EndY=6.5 EndZ=0
  constraints (53):
    c: Vertical(g0)
    c: Horizontal(g1)
    c: Vertical(g2)
    c: PointOnObject(g3,g-2)
    c: Horizontal(g3)
    c: Coincident(g3,g4)
    c: PointOnObject(g4,g-2)
    c: Coincident(g4,g5)
    c: Horizontal(g5)
    c: Vertical(g6)
    c: Coincident(g6,g7)
    c: Horizontal(g7)
    c: Coincident(g7,g8)
    c: Vertical(g8)
    c: Coincident(g8,g9)
    c: Coincident(g9,g0)
    c: Horizontal(g9)
    c: PointOnObject(g7,g-2)
    c: PointOnObject(g11,g1)
    c: PointOnObject(g11,g2)
    c: Tangent(g1,g10) = 1.5708
    c: Tangent(g2,g10) = 1.5708
    c: PointOnObject(g13,g3)
    c: PointOnObject(g13,g2)
    c: Tangent(g3,g12) = -1.5708
    c: Tangent(g2,g12) = -1.5708
    c: PointOnObject(g15,g1)
    c: PointOnObject(g15,g0)
    c: Tangent(g1,g14) = -1.5708
    c: Tangent(g0,g14) = -1.5708
    c: DistanceY(g1,g0) = 4
    c: DistanceX(g0,g2) = 10
    c: Equal(g14,g10)
    c: Radius(g14) = 2
    c: Coincident(g16,g17)
    c: Coincident(g17,g18)
    c: Coincident(g18,g19)
    c: Coincident(g19,g16)
    c: Vertical(g16)
    c: Vertical(g18)
    c: Horizontal(g17)
    c: Horizontal(g19)
    c: Coincident(g17,g-1)
    c: DistanceX(g6,g16) = 0.1
    c: DistanceY(g18,g7) = 0.1
    c: DistanceX(g17,g17) = 4.5
    c: DistanceY(g18,g18) = 6.5
    c: DistanceY(g-1,g8) = 41.5
    c: DistanceY(g4,g4) = 6
    c: DistanceY(g4,g17) = 0.1
    c: Coincident(g5,g6)
    c: Vertical(g12,g5)
    c: Radius(g12) = 2
FEATURE [PartDesign::Pad] Pad125
  Direction = (1,0,0)
  Length = 20
  Length2 = 10
  Midplane = true
  Placement = pos=(0,0,0) rot=(1,1,1;2.0944rad)
  Profile = -> Sketch263
  ReferenceAxis = -> Sketch263 [N_Axis]
  Suppressed = false
  Type = 0
FEATURE [Sketcher::SketchObject] Sketch264
  ArcFitTolerance = 1e-06
  AttachmentSupport = -> [XY_Plane289]
  ExternalGeometry = -> [Pad125]
  FullyConstrained = true
  MakeInternals = false
  MapMode = 5
  Placement = pos=(0,0,0) rot=(0,1,0;3.14159rad)
  sketch-geometry (8):
    g0: Circle CenterX=0 CenterY=-11.6 CenterZ=0 NormalX=0 NormalY=0 NormalZ=1 AngleXU=0 Radius=2.75
    g1: LineSegment [constr] StartX=-5e-16 StartY=-8.6 StartZ=0 EndX=5e-16 EndY=-14.6 EndZ=0
    g2: LineSegment [constr] StartX=4 StartY=-9.6 StartZ=0 EndX=4 EndY=-16.6 EndZ=0
    g3: LineSegment [constr] StartX=4 StartY=-16.6 StartZ=0 EndX=10 EndY=-16.6 EndZ=0
    g4: LineSegment [constr] StartX=10 StartY=-16.6 StartZ=0 EndX=10 EndY=-8.6 EndZ=0
    g5: LineSegment [constr] StartX=10 StartY=-8.6 StartZ=0 EndX=5 EndY=-8.6 EndZ=0
    g6: ArcOfCircle [constr] CenterX=5 CenterY=-9.6 CenterZ=0 NormalX=0 NormalY=0 NormalZ=1 AngleXU=0 Radius=1 StartAngle=1.5708 EndAngle=3.14159
    g7: GeomPoint [constr] X=4 Y=-8.6 Z=0
  constraints (21):
    c: PointOnObject(g1,g-3)
    c: PointOnObject(g1,g-4)
    c: Perpendicular(g-3,g1)
    c: Symmetric(g1,g1,g0)
    c: Diameter(g0) = 5.5
    c: Coincident(g2,g3)
    c: Coincident(g3,g4)
    c: Coincident(g4,g5)
    c: Vertical(g2)
    c: Vertical(g4)
    c: Horizontal(g3)
    c: Horizontal(g5)
    c: Coincident(g3,g-5)
    c: PointOnObject(g7,g5)
    c: PointOnObject(g7,g2)
    c: Tangent(g5,g6) = -1.5708
    c: Tangent(g2,g6) = -1.5708
    c: PointOnObject(g7,g-3)
    c: Radius(g6) = 1
    c: DistanceX(g0,g2) = 4
    c: PointOnObject(g0,g-2)
FEATURE [PartDesign::Pocket] Pocket112
  BaseFeature = -> Pad125
  Direction = (0,0,1)
  Length = 5
  Length2 = 5
  Placement = pos=(0,0,0) rot=(1,1,1;2.0944rad)
  Profile = -> Sketch264
  ReferenceAxis = -> Sketch264 [N_Axis]
  Suppressed = false
  Type = 1
FEATURE [Sketcher::SketchObject] Sketch265
  ArcFitTolerance = 1e-06
  AttachmentOffset = pos=(0,0,-6) rot=(0,0,1;0rad)
  AttachmentSupport = -> [Pocket112]
  FullyConstrained = true
  MakeInternals = false
  MapMode = 5
  Placement = pos=(0,-1.3e-15,-0.1) rot=(0.707107,0.707107,0;3.14159rad)
  sketch-geometry (1):
    g0: Circle CenterX=0 CenterY=-3.5 CenterZ=0 NormalX=0 NormalY=0 NormalZ=1 AngleXU=0 Radius=2.1
  constraints (3):
    c: Diameter(g0) = 4.2
    c: PointOnObject(g0,g-2)
    c: DistanceY(g0,g-1) = 3.5
FEATURE [PartDesign::Pocket] Pocket113
  BaseFeature = -> Pocket112
  Direction = (0,0,1)
  Length = 16
  Length2 = 5
  Placement = pos=(0,0,0) rot=(1,1,1;2.0944rad)
  Profile = -> Sketch265
  ReferenceAxis = -> Sketch265 [N_Axis]
  Reversed = true
  Suppressed = false
  Type = 0
FEATURE [Sketcher::SketchObject] Sketch266
  ArcFitTolerance = 1e-06
  AttachmentSupport = -> [XZ_Plane289]
  ExternalGeometry = -> [Pocket113]
  FullyConstrained = true
  MakeInternals = false
  MapMode = 5
  Placement = pos=(0,0,0) rot=(1,0,0;1.5708rad)
  sketch-geometry (6):
    g0: LineSegment StartX=10 StartY=-6.1 StartZ=0 EndX=10 EndY=35.5 EndZ=0
    g1: LineSegment StartX=10 StartY=35.5 StartZ=0 EndX=2 EndY=-6.1 EndZ=0
    g2: LineSegment StartX=2 StartY=-6.1 StartZ=0 EndX=10 EndY=-6.1 EndZ=0
    g3: LineSegment StartX=-8 StartY=35 StartZ=0 EndX=4.5 EndY=22.5 EndZ=0
    g4: LineSegment StartX=4.5 StartY=22.5 StartZ=0 EndX=-8 EndY=10 EndZ=0
    g5: LineSegment StartX=-8 StartY=35 StartZ=0 EndX=-8 EndY=10 EndZ=0
  constraints (16):
    c: Coincident(g1,g2)
    c: Coincident(g2,g0)
    c: Horizontal(g2)
    c: Coincident(g0,g-4)
    c: Coincident(g0,g-3)
    c: Coincident(g0,g1)
    c: DistanceX(g2,g2) = 8
    c: Coincident(g4,g3)
    c: Coincident(g5,g3)
    c: Coincident(g5,g4)
    c: Vertical(g5)
    c: Angle(g5,g3) = 0.785398
    c: Equal(g3,g4)
    c: DistanceX(g3,g-1) = 8
    c: DistanceY(g-1,g3) = 35
    c: DistanceY(g5,g5) = 25
FEATURE [PartDesign::Pocket] Pocket114
  BaseFeature = -> Pocket113
  Direction = (0,1,-2e-16)
  Length = 5
  Length2 = 5
  Midplane = true
  Placement = pos=(0,0,0) rot=(1,1,1;2.0944rad)
  Profile = -> Sketch266
  ReferenceAxis = -> Sketch266 [N_Axis]
  Suppressed = false
  Type = 1
FEATURE [PartDesign::Mirrored] Mirrored011
  BaseFeature = -> Pocket114
  MirrorPlane = -> XZ_Plane289
  Originals = -> [Pocket114]
  Placement = pos=(0,0,0) rot=(1,1,1;2.0944rad)
  Refine = true
  Suppressed = false
  TransformMode = 1
FEATURE [Sketcher::SketchObject] Sketch
  ArcFitTolerance = 1e-06
  AttachmentSupport = -> [Mirrored011]
  FullyConstrained = true
  MakeInternals = false
  MapMode = 5
  Placement = pos=(0,-5.3e-15,6.6) rot=(0.707107,0.707107,0;3.14159rad)
  sketch-geometry (1):
    g0: Circle CenterX=0 CenterY=-3.5 CenterZ=0 NormalX=0 NormalY=0 NormalZ=1 AngleXU=0 Radius=3.25
  constraints (3):
    c: Diameter(g0) = 6.5
    c: PointOnObject(g0,g-2)
    c: DistanceY(g0,g-1) = 3.5
FEATURE [PartDesign::Pocket] Pocket
  BaseFeature = -> Mirrored011
  Direction = (0,0,1)
  Length = 5
  Length2 = 5
  Placement = pos=(0,0,0) rot=(1,1,1;2.0944rad)
  Profile = -> Sketch
  ReferenceAxis = -> Sketch [N_Axis]
  Suppressed = false
  Type = 1
FEATURE [PartDesign::Body] Body089  label="support_rail_haut001"
  AllowCompound = false
  Group = -> [Sketch263,Pad125,Sketch264,Pocket112,Sketch265,Pocket113,Sketch266,Pocket114,Mirrored011,Sketch,Pocket]
  Origin = -> Origin292
  Placement = pos=(0,-2e-15,218) rot=(-0.707107,0,-0.707107;3.14159rad)
  Tip = -> Pocket
COMPONENT P10 — recipe-attached ("cale", modeled in this document).
Construction recipe (the document's own serialized feature program — sketch geometry with constraints, then the solid features built on it; lengths are millimeters unless a unit is written):

FEATURE [Sketcher::SketchObject] Sketch267
  ArcFitTolerance = 1e-06
  AttachmentSupport = -> [XZ_Plane290]
  FullyConstrained = true
  MakeInternals = false
  MapMode = 5
  Placement = pos=(0,0,0) rot=(1,0,0;1.5708rad)
  sketch-geometry (4):
    g0: LineSegment StartX=-4.5 StartY=0 StartZ=0 EndX=4.5 EndY=0 EndZ=0
    g1: LineSegment StartX=4.5 StartY=0 StartZ=0 EndX=4.5 EndY=2 EndZ=0
    g2: LineSegment StartX=4.5 StartY=2 StartZ=0 EndX=-4.5 EndY=2 EndZ=0
    g3: LineSegment StartX=-4.5 StartY=2 StartZ=0 EndX=-4.5 EndY=0 EndZ=0
  constraints (11):
    c: Coincident(g0,g1)
    c: Coincident(g1,g2)
    c: Coincident(g2,g3)
    c: Coincident(g3,g0)
    c: Horizontal(g0)
    c: Vertical(g1)
    c: Vertical(g3)
    c: PointOnObject(g0,g-1)
    c: Symmetric(g1,g2,g-2)
    c: Distance(g2,g2) = 9
    c: DistanceY(g3,g3) = 2
FEATURE [PartDesign::Pad] Pad126
  Direction = (0,-1,2e-16)
  Length = 40
  Length2 = 10
  Midplane = true
  Placement = pos=(0,0,0) rot=(1,0,0;1.5708rad)
  Profile = -> Sketch267
  ReferenceAxis = -> Sketch267 [N_Axis]
  Suppressed = false
  Type = 0
FEATURE [PartDesign::Body] Body090  label="cale"
  AllowCompound = false
  Group = -> [Sketch267,Pad126]
  Origin = -> Origin293
  Placement = pos=(71.5056,23,59.5) rot=(0.707107,0,0.707107;3.14159rad)
  Tip = -> Pad126
COMPONENT P11 — recipe-attached ("porte_cale", modeled in this document).
Construction recipe (the document's own serialized feature program — sketch geometry with constraints, then the solid features built on it; lengths are millimeters unless a unit is written):

FEATURE [Sketcher::SketchObject] Sketch215
  ArcFitTolerance = 1e-06
  AttachmentSupport = -> [XY_Plane291]
  FullyConstrained = true
  MakeInternals = false
  MapMode = 5
  expr: Constraints[2] = 16.5 mm / 2
  sketch-geometry (5):
    g0: Circle CenterX=-8.25 CenterY=0 CenterZ=0 NormalX=0 NormalY=0 NormalZ=1 AngleXU=0 Radius=2.1
    g1: ArcOfCircle CenterX=-8.25 CenterY=0 CenterZ=0 NormalX=0 NormalY=0 NormalZ=1 AngleXU=0 Radius=3 StartAngle=1.5708 EndAngle=4.71239
    g2: LineSegment StartX=0 StartY=-3 StartZ=0 EndX=-8.25 EndY=-3 EndZ=0
    g3: LineSegment StartX=0 StartY=3 StartZ=0 EndX=-8.25 EndY=3 EndZ=0
    g4: LineSegment StartX=0 StartY=3 StartZ=0 EndX=0 EndY=-3 EndZ=0
  constraints (13):
    c: Diameter(g0) = 4.2
    c: PointOnObject(g0,g-1)
    c: DistanceX(g0,g-1) = 8.25
    c: Tangent(g1,g2) = 1.5708
    c: Tangent(g1,g3) = -1.5708
    c: Horizontal(g3)
    c: Coincident(g1,g0)
    c: PointOnObject(g3,g-2)
    c: PointOnObject(g2,g-2)
    c: Coincident(g4,g3)
    c: Coincident(g4,g2)
    c: Horizontal(g2)
    c: Radius(g1) = 3
FEATURE [PartDesign::Pad] Pad110
  Direction = (0,0,1)
  Length = 15
  Length2 = 10
  Profile = -> Sketch215
  ReferenceAxis = -> Sketch215 [N_Axis]
  Suppressed = false
  Type = 0
FEATURE [Sketcher::SketchObject] Sketch216
  ArcFitTolerance = 1e-06
  AttachmentSupport = -> [XZ_Plane291]
  FullyConstrained = true
  MakeInternals = false
  MapMode = 5
  Placement = pos=(0,0,0) rot=(1,0,0;1.5708rad)
  sketch-geometry (6):
    g0: LineSegment StartX=-3.2536 StartY=15 StartZ=0 EndX=-3.11715 EndY=7.18255 EndZ=0
    g1: LineSegment StartX=0 StartY=6.2 StartZ=0 EndX=-2.1173 EndY=6.2 EndZ=0
    g2: LineSegment StartX=0 StartY=6.2 StartZ=0 EndX=0 EndY=15 EndZ=0
    g3: LineSegment StartX=-3.2536 StartY=15 StartZ=0 EndX=0 EndY=15 EndZ=0
    g4: ArcOfCircle CenterX=-2.1173 CenterY=7.2 CenterZ=0 NormalX=0 NormalY=0 NormalZ=1 AngleXU=0 Radius=1 StartAngle=3.15905 EndAngle=4.71239
    g5: GeomPoint [constr] X=-3.1 Y=6.2 Z=0
  constraints (16):
    c: PointOnObject(g1,g-2)
    c: Coincident(g2,g1)
    c: Vertical(g2)
    c: Coincident(g3,g0)
    c: Coincident(g3,g2)
    c: DistanceY(g-1,g1) = 6.2
    c: Horizontal(g3)
    c: DistanceY(g-1,g0) = 15
    c: Horizontal(g1)
    c: DistanceX(g5,g1) = 3.1
    c: PointOnObject(g5,g0)
    c: PointOnObject(g5,g1)
    c: Tangent(g0,g4) = -1.5708
    c: Tangent(g1,g4) = 1.5708
    c: Angle(g1,g0) = 1.58825
    c: Radius(g4) = 1
FEATURE [PartDesign::Pocket] Pocket079
  BaseFeature = -> Pad110
  Direction = (0,1,-2e-16)
  Length = 5
  Length2 = 5
  Midplane = true
  Profile = -> Sketch216
  ReferenceAxis = -> Sketch216 [N_Axis]
  Suppressed = false
  Type = 1
FEATURE [Sketcher::SketchObject] Sketch268
  ArcFitTolerance = 1e-06
  AttachmentSupport = -> [XZ_Plane291]
  ExternalGeometry = -> [Pocket079]
  FullyConstrained = true
  MakeInternals = false
  MapMode = 5
  Placement = pos=(0,0,0) rot=(1,0,0;1.5708rad)
  sketch-geometry (3):
    g0: LineSegment StartX=-12 StartY=8 StartZ=0 EndX=-5 EndY=15 EndZ=0
    g1: LineSegment StartX=-12 StartY=15 StartZ=0 EndX=-12 EndY=8 EndZ=0
    g2: LineSegment StartX=-5 StartY=15 StartZ=0 EndX=-12 EndY=15 EndZ=0
  constraints (9):
    c: Vertical(g1)
    c: Coincident(g1,g2)
    c: Coincident(g0,g2)
    c: Coincident(g0,g1)
    c: Horizontal(g2)
    c: Horizontal(g2,g-3)
    c: DistanceX(g1,g-1) = 12
    c: Angle(g0,g1) = 0.785398
    c: DistanceX(g2,g2) = 7
FEATURE [PartDesign::Pocket] Pocket115
  BaseFeature = -> Pocket079
  Direction = (0,1,-2e-16)
  Length = 5
  Length2 = 5
  Midplane = true
  Profile = -> Sketch268
  ReferenceAxis = -> Sketch268 [N_Axis]
  Suppressed = false
  Type = 1
FEATURE [PartDesign::Mirrored] Mirrored046
  BaseFeature = -> Pocket115
  MirrorPlane = -> Sketch216 [V_Axis]
  Originals = -> [Pocket079]
  Suppressed = false
  TransformMode = 1
FEATURE [PartDesign::Body] Body091  label="porte_cale"
  AllowCompound = false
  Group = -> [Sketch215,Pad110,Sketch216,Pocket079,Sketch268,Pocket115,Mirrored046]
  Origin = -> Origin294
  Placement = pos=(71.5,19.83,20) rot=(-0.707107,-0.707107,0;3.14159rad)
  Tip = -> Mirrored046
COMPONENT P12 — geometry summary ("L16_50MM_SW_ASM"; no construction recipe available for this part):
  bounding box: 126.4 x 26.1 x 20.0 mm
  tessellated surface: 52,840 triangles
  volume: 16350 mm^3 (25% of its bounding box)
COMPONENT P13 — same part as P4; its construction recipe is shown at P4.
COMPONENT P14 — same part as P8; its construction recipe is shown at P8.
COMPONENT P15 — recipe-attached ("Hiwin MGN9", modeled in this document).
Construction recipe (the document's own serialized feature program — sketch geometry with constraints, then the solid features built on it; lengths are millimeters unless a unit is written):

FEATURE [Sketcher::SketchObject] Sketch031
  ArcFitTolerance = 0
  AttachmentSupport = -> [YZ_Plane013]
  FullyConstrained = true
  MakeInternals = false
  MapMode = 5
  Placement = pos=(0,0,0) rot=(0.57735,0.57735,0.57735;2.0944rad)
  sketch-geometry (4):
    g0: LineSegment StartX=-4.5 StartY=0 StartZ=0 EndX=4.5 EndY=0 EndZ=0
    g1: LineSegment StartX=4.5 StartY=0 StartZ=0 EndX=4.5 EndY=6.5 EndZ=0
    g2: LineSegment StartX=4.5 StartY=6.5 StartZ=0 EndX=-4.5 EndY=6.5 EndZ=0
    g3: LineSegment StartX=-4.5 StartY=6.5 StartZ=0 EndX=-4.5 EndY=0 EndZ=0
  constraints (11):
    c: Coincident(g0,g1)
    c: Coincident(g1,g2)
    c: Coincident(g2,g3)
    c: Coincident(g3,g0)
    c: Horizontal(g0)
    c: Horizontal(g2)
    c: Vertical(g1)
    c: Vertical(g3)
    c: Symmetric(g0,g0,g-1)
    c: DistanceX(g0,g0) = 9  'width'
    c: DistanceY(g1,g1) = 6.5  'height'
FEATURE [PartDesign::Pad] Pad012
  Direction = (1,0,0)
  Length = 215
  Length2 = 10
  Placement = pos=(0,0,0) rot=(0.57735,0.57735,0.57735;2.0944rad)
  Profile = -> Sketch031
  ReferenceAxis = -> Sketch031 [N_Axis]
  Suppressed = false
  Type = 0
  expr: Length = Spreadsheet001.length
FEATURE [Sketcher::SketchObject] Sketch032
  ArcFitTolerance = 0
  AttachmentSupport = -> [YZ_Plane013]
  FullyConstrained = true
  MakeInternals = false
  MapMode = 5
  Placement = pos=(0,0,0) rot=(0.57735,-0.57735,-0.57735;2.0944rad)
  expr: Constraints[13] = 6.5 - 1.8
  expr: Constraints[14] = <<Sketch031>>.Constraints.width / 2 + 0.1 mm
  sketch-geometry (10):
    g0: ArcOfCircle CenterX=-4.6 CenterY=4.7 CenterZ=0 NormalX=0 NormalY=0 NormalZ=1 AngleXU=0 Radius=1 StartAngle=0.25268 EndAngle=6.03051
    g1: LineSegment StartX=-3.63175 StartY=4.95 StartZ=0 EndX=-3.13175 EndY=4.95 EndZ=0
    g2: LineSegment StartX=-3.13175 StartY=4.95 StartZ=0 EndX=-3.13175 EndY=4.45 EndZ=0
    g3: LineSegment StartX=-3.13175 StartY=4.45 StartZ=0 EndX=-3.63175 EndY=4.45 EndZ=0
    g4: LineSegment [constr] StartX=-4.6 StartY=4.7 StartZ=0 EndX=-3.13175 EndY=4.7 EndZ=0
    g5: ArcOfCircle CenterX=4.6 CenterY=4.7 CenterZ=0 NormalX=0 NormalY=0 NormalZ=1 AngleXU=0 Radius=1 StartAngle=3.39427 EndAngle=9.1721
    g6: LineSegment StartX=3.63175 StartY=4.95 StartZ=0 EndX=3.13175 EndY=4.95 EndZ=0
    g7: LineSegment StartX=3.13175 StartY=4.95 StartZ=0 EndX=3.13175 EndY=4.45 EndZ=0
    g8: LineSegment StartX=3.13175 StartY=4.45 StartZ=0 EndX=3.63175 EndY=4.45 EndZ=0
    g9: LineSegment [constr] StartX=4.6 StartY=4.7 StartZ=0 EndX=3.13175 EndY=4.7 EndZ=0
  constraints (29):
    c: Horizontal(g1)
    c: Coincident(g2,g1)
    c: Vertical(g2)
    c: Coincident(g3,g2)
    c: Horizontal(g3)
    c: Coincident(g4,g0)
    c: Horizontal(g4)
    c: Symmetric(g2,g1,g4)
    c: Coincident(g0,g3)
    c: Coincident(g0,g1)
    c: DistanceY(g2,g2) = 0.5
    c: DistanceX(g1,g1) = 0.5
    c: Diameter(g0) = 2
    c: DistanceY(g-1,g0) = 4.7
    c: DistanceX(g0,g-1) = 4.6
    c: Horizontal(g6)
    c: Coincident(g7,g6)
    c: Vertical(g7)
    c: Coincident(g8,g7)
    c: Horizontal(g8)
    c: Coincident(g9,g5)
    c: Horizontal(g9)
    c: Symmetric(g7,g6,g9)
    c: Coincident(g5,g8)
    c: Coincident(g5,g6)
    c: Diameter(g5) = 2
    c: Symmetric(g4,g9,g-2)
    c: Equal(g2,g7)
    c: Equal(g1,g6)
FEATURE [PartDesign::Pocket] Pocket015  label="Balls cut"
  BaseFeature = -> Pad012
  Direction = (1,0,0)
  Length = 5
  Length2 = 5
  Placement = pos=(0,0,0) rot=(0.57735,0.57735,0.57735;2.0944rad)
  Profile = -> Sketch032
  ReferenceAxis = -> Sketch032 [N_Axis]
  Suppressed = false
  Type = 1
FEATURE [Sketcher::SketchObject] Sketch033
  ArcFitTolerance = 0
  AttachmentOffset = pos=(5.5,0,0) rot=(0,0,1;1.5708rad)
  AttachmentSupport = -> [XY_Plane013]
  FullyConstrained = true
  MakeInternals = false
  MapMode = 5
  Placement = pos=(5.5,0,0) rot=(0,0,1;1.5708rad)
  expr: .AttachmentOffset.Base.x = Spreadsheet001.offset
  sketch-geometry (1):
    g0: Circle CenterX=0 CenterY=0 CenterZ=0 NormalX=0 NormalY=0 NormalZ=1 AngleXU=0 Radius=1.75
  constraints (2):
    c: Coincident(g0,g-1)
    c: Diameter(g0) = 3.5
FEATURE [PartDesign::Pocket] Pocket016  label="Screw hole"
  BaseFeature = -> Pocket015
  Direction = (0,0,-1)
  Length = 5
  Length2 = 5
  Midplane = true
  Placement = pos=(0,0,0) rot=(0.57735,0.57735,0.57735;2.0944rad)
  Profile = -> Sketch033
  ReferenceAxis = -> Sketch033 [N_Axis]
  Suppressed = false
  Type = 1
FEATURE [Sketcher::SketchObject] Sketch034
  ArcFitTolerance = 0
  AttachmentOffset = pos=(5.5,0,6.5) rot=(0,0,1;1.5708rad)
  AttachmentSupport = -> [XY_Plane013]
  FullyConstrained = true
  MakeInternals = false
  MapMode = 5
  Placement = pos=(5.5,0,6.5) rot=(0,0,1;1.5708rad)
  expr: .AttachmentOffset.Base.x = Spreadsheet001.offset
  expr: .AttachmentOffset.Base.z = Sketch031.Constraints.height
  sketch-geometry (1):
    g0: Circle CenterX=0 CenterY=0 CenterZ=0 NormalX=0 NormalY=0 NormalZ=1 AngleXU=0 Radius=3
  constraints (2):
    c: Coincident(g0,g-1)
    c: Diameter(g0) = 6
FEATURE [PartDesign::Pocket] Pocket017  label="Screw head cut"
  BaseFeature = -> Pocket016
  Direction = (0,0,-1)
  Length = 3.5
  Length2 = 5
  Placement = pos=(0,0,0) rot=(0.57735,0.57735,0.57735;2.0944rad)
  Profile = -> Sketch034
  ReferenceAxis = -> Sketch034 [N_Axis]
  Suppressed = false
  Type = 0
FEATURE [PartDesign::Chamfer] Chamfer001  label="Chamfer"
  Angle = 45
  Base = -> Pocket017 [Edge47]
  BaseFeature = -> Pocket017
  ChamferType = 0
  FlipDirection = false
  Placement = pos=(0,0,0) rot=(0.57735,0.57735,0.57735;2.0944rad)
  Size = 0.2
  Size2 = 1
  SupportTransform = false
  Suppressed = false
  UseAllEdges = false
FEATURE [PartDesign::LinearPattern] LinearPattern001  label="LinearPattern"
  BaseFeature = -> Chamfer001
  Direction = -> Sketch033 [V_Axis]
  Length = 200
  Mode = 0
  Occurrences = 11
  Offset = 20
  Originals = -> [Pocket016,Pocket017,Chamfer001]
  Placement = pos=(0,0,0) rot=(0.57735,0.57735,0.57735;2.0944rad)
  Reversed = true
  Suppressed = false
  TransformMode = 0
  expr: Length = Spreadsheet001.distance
  expr: Occurrences = Spreadsheet001.holes_number
FEATURE [PartDesign::Body] Body011  label="Hiwin rail MGN9R"
  AllowCompound = false
  Group = -> [Sketch031,Pad012,Sketch032,Pocket015,Sketch033,Pocket016,Sketch034,Pocket017,Chamfer001,LinearPattern001]
  Origin = -> Origin013
  Tip = -> LinearPattern001
COMPONENT P16 — geometry summary ("Partie mobile"; no construction recipe available for this part):
  bounding box: 87.0 x 46.3 x 29.0 mm
  tessellated surface: 32,602 triangles
  volume: 28165 mm^3 (24% of its bounding box)
COMPONENT P17 — recipe-attached ("servo_DS3218MG003", modeled in this document).
Construction recipe (the document's own serialized feature program — sketch geometry with constraints, then the solid features built on it; lengths are millimeters unless a unit is written):

FEATURE [Sketcher::SketchObject] Sketch260
  ArcFitTolerance = 0
  AttachmentSupport = -> [XZ_Plane288]
  FullyConstrained = true
  MakeInternals = false
  MapMode = 5
  Placement = pos=(0,0,0) rot=(1,0,0;1.5708rad)
  expr: Constraints[19] = 19.8 / 2
  sketch-geometry (8):
    g0: LineSegment StartX=2.5 StartY=3.4 StartZ=0 EndX=2.5 EndY=0 EndZ=0
    g1: LineSegment StartX=2.5 StartY=0 StartZ=0 EndX=4.2 EndY=0 EndZ=0
    g2: LineSegment StartX=4.2 StartY=0 StartZ=0 EndX=4.2 EndY=2 EndZ=0
    g3: LineSegment StartX=4.2 StartY=2 StartZ=0 EndX=9.9 EndY=2 EndZ=0
    g4: LineSegment StartX=9.9 StartY=2 StartZ=0 EndX=9.9 EndY=4.4 EndZ=0
    g5: LineSegment StartX=9.9 StartY=4.4 StartZ=0 EndX=1.5 EndY=4.4 EndZ=0
    g6: LineSegment StartX=1.5 StartY=4.4 StartZ=0 EndX=1.5 EndY=3.4 EndZ=0
    g7: LineSegment StartX=1.5 StartY=3.4 StartZ=0 EndX=2.5 EndY=3.4 EndZ=0
  constraints (24):
    c: PointOnObject(g0,g-1)
    c: Vertical(g0)
    c: Coincident(g1,g0)
    c: PointOnObject(g1,g-1)
    c: Coincident(g2,g1)
    c: Vertical(g2)
    c: Coincident(g3,g2)
    c: Horizontal(g3)
    c: Coincident(g4,g3)
    c: Vertical(g4)
    c: Coincident(g5,g4)
    c: Horizontal(g5)
    c: Coincident(g6,g5)
    c: Coincident(g7,g6)
    c: Coincident(g7,g0)
    c: Horizontal(g7)
    c: Vertical(g6)
    c: DistanceY(g4,g4) = 2.4
    c: DistanceY(g2,g2) = 2
    c: DistanceX(g-1,g4) = 9.9
    c: DistanceX(g-1,g6) = 1.5
    c: DistanceY(g0,g0) = 3.4
    c: DistanceX(g-1,g0) = 2.5
    c: DistanceX(g1,g1) = 1.7
FEATURE [PartDesign::Revolution] Revolution002
  Angle = 360
  Angle2 = 60
  Axis = (0,2e-16,1)
  Base = (0,0,0)
  Placement = pos=(0,0,0) rot=(1,0,0;1.5708rad)
  Profile = -> Sketch260
  ReferenceAxis = -> Sketch260 [V_Axis]
  Reversed = true
  Suppressed = false
  Type = 0
FEATURE [Sketcher::SketchObject] Sketch261
  ArcFitTolerance = 0
  AttachmentSupport = -> [XY_Plane288]
  FullyConstrained = true
  MakeInternals = false
  MapMode = 5
  sketch-geometry (1):
    g0: Circle CenterX=-7 CenterY=0 CenterZ=0 NormalX=0 NormalY=0 NormalZ=1 AngleXU=0 Radius=1.2
  constraints (3):
    c: PointOnObject(g0,g-1)
    c: Diameter(g0) = 2.4
    c: DistanceX(g0,g-1) = 7
FEATURE [PartDesign::Pocket] Pocket111
  BaseFeature = -> Revolution002
  Direction = (0,0,-1)
  Length = 5
  Length2 = 5
  Midplane = true
  Placement = pos=(0,0,0) rot=(1,0,0;1.5708rad)
  Profile = -> Sketch261
  ReferenceAxis = -> Sketch261 [N_Axis]
  Suppressed = false
  Type = 1
FEATURE [PartDesign::PolarPattern] PolarPattern006
  Angle = 360
  Axis = -> Sketch261 [N_Axis]
  BaseFeature = -> Pocket111
  Mode = 0
  Occurrences = 4
  Offset = 120
  Originals = -> [Pocket111]
  Placement = pos=(0,0,0) rot=(1,0,0;1.5708rad)
  Suppressed = false
  TransformMode = 0
FEATURE [PartDesign::Body] Body010  label="Corps002"
  AllowCompound = false
  Group = -> [Sketch260,Revolution002,Sketch261,Pocket111,PolarPattern006]
  Origin = -> Origin291
  Placement = pos=(0,0,0.4) rot=(0,0,1;0rad)
  Tip = -> PolarPattern006
PROVENANCE & LICENSES
A FreeCAD (.FCStd) document from a public repository crawl; recipes are the document's own serialized feature recipes (and, for linked parts, companion documents' recipes).
License: as declared in the source repository (recorded in the dataset sidecar).
